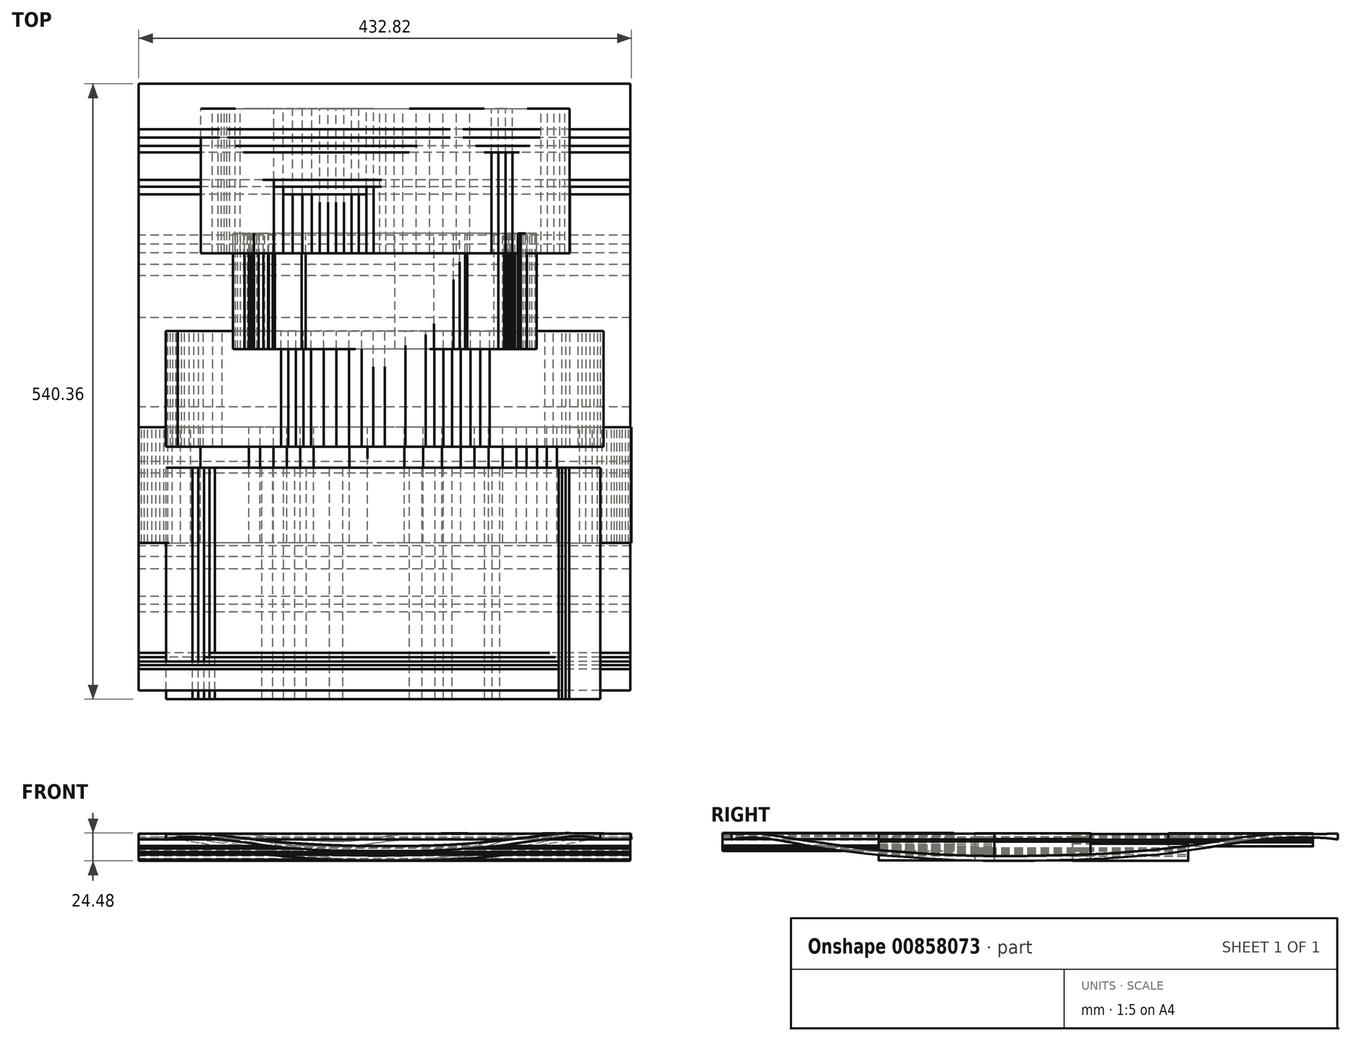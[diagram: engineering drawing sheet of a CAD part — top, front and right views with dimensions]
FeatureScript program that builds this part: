
annotation { "Feature Type Name" : "Feature", "Feature Type Description" : "" }
export const myFeature = defineFeature(function(context is Context, id is Id, definition is map)
    precondition{}
    {
        {
            var Q0;
            Q0=qCreatedBy(makeId("Top.planeOp"),FACE);
            var sketch = newSketch(context, id + "F0", { "sketchPlane" : qUnion([Q0])});
            skLineSegment(sketch, "E0", {"start": v(-117.35, 265.42) * mm, "end": v(-117.3, 265.42) * mm});
            skLineSegment(sketch, "E1", {"start": v(-117.3, 265.42) * mm, "end": v(-117.19, 265.42) * mm});
            skLineSegment(sketch, "E2", {"start": v(-117.19, 265.42) * mm, "end": v(-117.15, 265.42) * mm});
            skLineSegment(sketch, "E3", {"start": v(-117.15, 265.42) * mm, "end": v(-112.35, 265.42) * mm});
            skLineSegment(sketch, "E4", {"start": v(-112.35, 265.42) * mm, "end": v(-97.96, 264.94) * mm});
            skLineSegment(sketch, "E5", {"start": v(-97.96, 264.94) * mm, "end": v(-82, 263.83) * mm});
            skLineSegment(sketch, "E6", {"start": v(-82, 263.83) * mm, "end": v(-78.82, 263.51) * mm});
            skLineSegment(sketch, "E7", {"start": v(-78.82, 263.51) * mm, "end": v(-75.82, 263.23) * mm});
            skLineSegment(sketch, "E8", {"start": v(-75.82, 263.23) * mm, "end": v(-60.94, 260.85) * mm});
            skLineSegment(sketch, "E9", {"start": v(-60.94, 260.85) * mm, "end": v(-46.33, 257.18) * mm});
            skLineSegment(sketch, "E10", {"start": v(-46.33, 257.18) * mm, "end": v(-43.46, 256.25) * mm});
            skLineSegment(sketch, "E11", {"start": v(-43.46, 256.25) * mm, "end": v(-41.7, 255.72) * mm});
            skLineSegment(sketch, "E12", {"start": v(-41.7, 255.72) * mm, "end": v(-36.48, 253.85) * mm});
            skLineSegment(sketch, "E13", {"start": v(-36.48, 253.85) * mm, "end": v(-29.74, 250.92) * mm});
            skLineSegment(sketch, "E14", {"start": v(-29.74, 250.92) * mm, "end": v(-23.27, 247.49) * mm});
            skLineSegment(sketch, "E15", {"start": v(-23.27, 247.49) * mm, "end": v(-17.09, 243.56) * mm});
            skLineSegment(sketch, "E16", {"start": v(-17.09, 243.56) * mm, "end": v(-11.24, 239.16) * mm});
            skLineSegment(sketch, "E17", {"start": v(-11.24, 239.16) * mm, "end": v(-5.74, 234.32) * mm});
            skLineSegment(sketch, "E18", {"start": v(-5.74, 234.32) * mm, "end": v(-0.63, 229.04) * mm});
            skLineSegment(sketch, "E19", {"start": v(-0.63, 229.04) * mm, "end": v(2.96, 224.81) * mm});
            skLineSegment(sketch, "E20", {"start": v(2.96, 224.81) * mm, "end": v(4.08, 223.34) * mm});
            skLineSegment(sketch, "E21", {"start": v(4.08, 223.34) * mm, "end": v(5.7, 220.98) * mm});
            skLineSegment(sketch, "E22", {"start": v(5.7, 220.98) * mm, "end": v(9.84, 213.38) * mm});
            skLineSegment(sketch, "E23", {"start": v(9.84, 213.38) * mm, "end": v(14.01, 202.73) * mm});
            skLineSegment(sketch, "E24", {"start": v(14.01, 202.73) * mm, "end": v(16.56, 191.58) * mm});
            skLineSegment(sketch, "E25", {"start": v(16.56, 191.58) * mm, "end": v(17.43, 182.97) * mm});
            skLineSegment(sketch, "E26", {"start": v(17.43, 182.97) * mm, "end": v(17.43, 180.1) * mm});
            skLineSegment(sketch, "E27", {"start": v(17.43, 180.1) * mm, "end": v(17.43, 177.1) * mm});
            skLineSegment(sketch, "E28", {"start": v(17.43, 177.1) * mm, "end": v(16.64, 169.08) * mm});
            skLineSegment(sketch, "E29", {"start": v(16.64, 169.08) * mm, "end": v(16.48, 168.08) * mm});
            skLineSegment(sketch, "E30", {"start": v(16.48, 168.08) * mm, "end": v(15.89, 164.58) * mm});
            skLineSegment(sketch, "E31", {"start": v(15.89, 164.58) * mm, "end": v(13.52, 154.18) * mm});
            skLineSegment(sketch, "E32", {"start": v(13.52, 154.18) * mm, "end": v(9.43, 140.6) * mm});
            skLineSegment(sketch, "E33", {"start": v(9.43, 140.6) * mm, "end": v(4.22, 127.4) * mm});
            skLineSegment(sketch, "E34", {"start": v(4.22, 127.4) * mm, "end": v(-0.38, 117.78) * mm});
            skLineSegment(sketch, "E35", {"start": v(-0.38, 117.78) * mm, "end": v(-2.1, 114.67) * mm});
            skLineSegment(sketch, "E36", {"start": v(-10.33, 95.13) * mm, "end": v(-9.83, 96.82) * mm});
            skLineSegment(sketch, "E37", {"start": v(-9.83, 96.82) * mm, "end": v(-6.75, 105.13) * mm});
            skLineSegment(sketch, "E38", {"start": v(-6.75, 105.13) * mm, "end": v(-2.96, 113.12) * mm});
            skLineSegment(sketch, "E39", {"start": v(-2.96, 113.12) * mm, "end": v(-2.1, 114.67) * mm});
            skLineSegment(sketch, "E40", {"start": v(-10.57, 72.87) * mm, "end": v(-10.76, 73.74) * mm});
            skLineSegment(sketch, "E41", {"start": v(-10.76, 73.74) * mm, "end": v(-11.73, 81.05) * mm});
            skLineSegment(sketch, "E42", {"start": v(-11.73, 81.05) * mm, "end": v(-11.73, 83.49) * mm});
            skLineSegment(sketch, "E43", {"start": v(-11.73, 83.49) * mm, "end": v(-11.73, 84.95) * mm});
            skLineSegment(sketch, "E44", {"start": v(-11.73, 84.95) * mm, "end": v(-11.38, 89.35) * mm});
            skLineSegment(sketch, "E45", {"start": v(-11.38, 89.35) * mm, "end": v(-10.57, 94.17) * mm});
            skLineSegment(sketch, "E46", {"start": v(-10.57, 94.17) * mm, "end": v(-10.33, 95.13) * mm});
            skLineSegment(sketch, "E47", {"start": v(-3.12, 55.92) * mm, "end": v(-3.8, 56.87) * mm});
            skLineSegment(sketch, "E48", {"start": v(-3.8, 56.87) * mm, "end": v(-5.64, 59.85) * mm});
            skLineSegment(sketch, "E49", {"start": v(-5.64, 59.85) * mm, "end": v(-7.73, 64) * mm});
            skLineSegment(sketch, "E50", {"start": v(-7.73, 64) * mm, "end": v(-9.38, 68.36) * mm});
            skLineSegment(sketch, "E51", {"start": v(-9.38, 68.36) * mm, "end": v(-10.33, 71.73) * mm});
            skLineSegment(sketch, "E52", {"start": v(-10.33, 71.73) * mm, "end": v(-10.57, 72.87) * mm});
            skLineSegment(sketch, "E53", {"start": v(15.48, 34.95) * mm, "end": v(13.8, 36.58) * mm});
            skLineSegment(sketch, "E54", {"start": v(13.8, 36.58) * mm, "end": v(5.8, 45.1) * mm});
            skLineSegment(sketch, "E55", {"start": v(5.8, 45.1) * mm, "end": v(-1.7, 54.06) * mm});
            skLineSegment(sketch, "E56", {"start": v(-1.7, 54.06) * mm, "end": v(-3.12, 55.92) * mm});
            skLineSegment(sketch, "E57", {"start": v(15.48, 34.95) * mm, "end": v(15.65, 34.77) * mm});
            skLineSegment(sketch, "E58", {"start": v(15.65, 34.77) * mm, "end": v(17.37, 33) * mm});
            skLineSegment(sketch, "E59", {"start": v(17.37, 33) * mm, "end": v(17.54, 32.82) * mm});
            skLineSegment(sketch, "E60", {"start": v(19.48, 30.83) * mm, "end": v(19.32, 31) * mm});
            skLineSegment(sketch, "E61", {"start": v(19.32, 31) * mm, "end": v(17.7, 32.65) * mm});
            skLineSegment(sketch, "E62", {"start": v(17.7, 32.65) * mm, "end": v(17.54, 32.82) * mm});
            skLineSegment(sketch, "E63", {"start": v(19.48, 30.83) * mm, "end": v(21.7, 28.6) * mm});
            skLineSegment(sketch, "E64", {"start": v(21.7, 28.6) * mm, "end": v(28.13, 21.67) * mm});
            skLineSegment(sketch, "E65", {"start": v(28.13, 21.67) * mm, "end": v(36.2, 12) * mm});
            skLineSegment(sketch, "E66", {"start": v(36.2, 12) * mm, "end": v(43.68, 1.88) * mm});
            skLineSegment(sketch, "E67", {"start": v(43.68, 1.88) * mm, "end": v(48.9, -6) * mm});
            skLineSegment(sketch, "E68", {"start": v(48.9, -6) * mm, "end": v(50.53, -8.7) * mm});
            skLineSegment(sketch, "E69", {"start": v(50.53, -8.7) * mm, "end": v(52.29, -11.77) * mm});
            skLineSegment(sketch, "E70", {"start": v(52.29, -11.77) * mm, "end": v(57, -21.33) * mm});
            skLineSegment(sketch, "E71", {"start": v(57, -21.33) * mm, "end": v(62.25, -34.49) * mm});
            skLineSegment(sketch, "E72", {"start": v(62.25, -34.49) * mm, "end": v(66.25, -48.08) * mm});
            skLineSegment(sketch, "E73", {"start": v(66.25, -48.08) * mm, "end": v(68.46, -58.5) * mm});
            skLineSegment(sketch, "E74", {"start": v(68.46, -58.5) * mm, "end": v(68.98, -62.01) * mm});
            skLineSegment(sketch, "E75", {"start": v(68.98, -62.01) * mm, "end": v(69.27, -64.04) * mm});
            skLineSegment(sketch, "E76", {"start": v(69.27, -64.04) * mm, "end": v(70.32, -74.23) * mm});
            skLineSegment(sketch, "E77", {"start": v(70.32, -74.23) * mm, "end": v(70.76, -83.45) * mm});
            skLineSegment(sketch, "E78", {"start": v(70.76, -83.45) * mm, "end": v(70.76, -86.52) * mm});
            skLineSegment(sketch, "E79", {"start": v(70.76, -86.52) * mm, "end": v(70.76, -89.59) * mm});
            skLineSegment(sketch, "E80", {"start": v(70.76, -89.59) * mm, "end": v(70.32, -98.8) * mm});
            skLineSegment(sketch, "E81", {"start": v(70.32, -98.8) * mm, "end": v(68.99, -110.98) * mm});
            skLineSegment(sketch, "E82", {"start": v(68.99, -110.98) * mm, "end": v(66.78, -122.99) * mm});
            skLineSegment(sketch, "E83", {"start": v(66.78, -122.99) * mm, "end": v(63.72, -134.8) * mm});
            skLineSegment(sketch, "E84", {"start": v(63.72, -134.8) * mm, "end": v(59.81, -146.35) * mm});
            skLineSegment(sketch, "E85", {"start": v(59.81, -146.35) * mm, "end": v(55.08, -157.61) * mm});
            skLineSegment(sketch, "E86", {"start": v(55.08, -157.61) * mm, "end": v(49.52, -168.53) * mm});
            skLineSegment(sketch, "E87", {"start": v(49.52, -168.53) * mm, "end": v(44.85, -176.48) * mm});
            skLineSegment(sketch, "E88", {"start": v(44.85, -176.48) * mm, "end": v(43.17, -179.05) * mm});
            skLineSegment(sketch, "E89", {"start": v(43.17, -179.05) * mm, "end": v(40.83, -182.6) * mm});
            skLineSegment(sketch, "E90", {"start": v(40.83, -182.6) * mm, "end": v(33.17, -192.84) * mm});
            skLineSegment(sketch, "E91", {"start": v(33.17, -192.84) * mm, "end": v(22.02, -205.57) * mm});
            skLineSegment(sketch, "E92", {"start": v(22.02, -205.57) * mm, "end": v(9.8, -217.2) * mm});
            skLineSegment(sketch, "E93", {"start": v(9.8, -217.2) * mm, "end": v(-3.38, -227.64) * mm});
            skLineSegment(sketch, "E94", {"start": v(-3.38, -227.64) * mm, "end": v(-17.46, -236.86) * mm});
            skLineSegment(sketch, "E95", {"start": v(-17.46, -236.86) * mm, "end": v(-32.35, -244.77) * mm});
            skLineSegment(sketch, "E96", {"start": v(-32.35, -244.77) * mm, "end": v(-47.95, -251.32) * mm});
            skLineSegment(sketch, "E97", {"start": v(-47.95, -251.32) * mm, "end": v(-60.08, -255.36) * mm});
            skLineSegment(sketch, "E98", {"start": v(-60.08, -255.36) * mm, "end": v(-64.2, -256.46) * mm});
            skLineSegment(sketch, "E99", {"start": v(-64.2, -256.46) * mm, "end": v(-68.82, -257.57) * mm});
            skLineSegment(sketch, "E100", {"start": v(-68.82, -257.57) * mm, "end": v(-82.83, -260.37) * mm});
            skLineSegment(sketch, "E101", {"start": v(-82.83, -260.37) * mm, "end": v(-101.65, -263.17) * mm});
            skLineSegment(sketch, "E102", {"start": v(-101.65, -263.17) * mm, "end": v(-120.6, -264.86) * mm});
            skLineSegment(sketch, "E103", {"start": v(-120.6, -264.86) * mm, "end": v(-134.88, -265.42) * mm});
            skLineSegment(sketch, "E104", {"start": v(-134.88, -265.42) * mm, "end": v(-139.63, -265.42) * mm});
            skLineSegment(sketch, "E105", {"start": v(-139.63, -265.42) * mm, "end": v(-141.04, -265.42) * mm});
            skLineSegment(sketch, "E106", {"start": v(-141.04, -265.42) * mm, "end": v(-144.77, -265.38) * mm});
            skLineSegment(sketch, "E107", {"start": v(-144.77, -265.38) * mm, "end": v(-145.24, -265.37) * mm});
            skLineSegment(sketch, "E108", {"start": v(-145.24, -265.37) * mm, "end": v(-145.37, -265.37) * mm});
            skLineSegment(sketch, "E109", {"start": v(-145.37, -265.37) * mm, "end": v(-146.47, -265.37) * mm});
            skLineSegment(sketch, "E110", {"start": v(-146.47, -265.37) * mm, "end": v(-146.83, -265.37) * mm});
            skLineSegment(sketch, "E111", {"start": v(-146.83, -265.37) * mm, "end": v(-152.93, -265.37) * mm});
            skLineSegment(sketch, "E112", {"start": v(-152.93, -265.37) * mm, "end": v(-171.22, -264.53) * mm});
            skLineSegment(sketch, "E113", {"start": v(-171.22, -264.53) * mm, "end": v(-191.46, -262.56) * mm});
            skLineSegment(sketch, "E114", {"start": v(-191.46, -262.56) * mm, "end": v(-195.48, -262) * mm});
            skLineSegment(sketch, "E115", {"start": v(-195.48, -262) * mm, "end": v(-198.88, -261.62) * mm});
            skLineSegment(sketch, "E116", {"start": v(-198.88, -261.62) * mm, "end": v(-209, -260.03) * mm});
            skLineSegment(sketch, "E117", {"start": v(-209, -260.03) * mm, "end": v(-222.3, -257.15) * mm});
            skLineSegment(sketch, "E118", {"start": v(-222.3, -257.15) * mm, "end": v(-235.35, -253.4) * mm});
            skLineSegment(sketch, "E119", {"start": v(-235.35, -253.4) * mm, "end": v(-248.1, -248.77) * mm});
            skLineSegment(sketch, "E120", {"start": v(-248.1, -248.77) * mm, "end": v(-260.5, -243.3) * mm});
            skLineSegment(sketch, "E121", {"start": v(-260.5, -243.3) * mm, "end": v(-272.53, -236.98) * mm});
            skLineSegment(sketch, "E122", {"start": v(-272.53, -236.98) * mm, "end": v(-284.12, -229.86) * mm});
            skLineSegment(sketch, "E123", {"start": v(-284.12, -229.86) * mm, "end": v(-292.53, -224) * mm});
            skLineSegment(sketch, "E124", {"start": v(-292.53, -224) * mm, "end": v(-295.24, -221.94) * mm});
            skLineSegment(sketch, "E125", {"start": v(-295.24, -221.94) * mm, "end": v(-297.42, -220.16) * mm});
            skLineSegment(sketch, "E126", {"start": v(-297.42, -220.16) * mm, "end": v(-303.74, -214.56) * mm});
            skLineSegment(sketch, "E127", {"start": v(-303.74, -214.56) * mm, "end": v(-311.75, -206.7) * mm});
            skLineSegment(sketch, "E128", {"start": v(-311.75, -206.7) * mm, "end": v(-319.24, -198.37) * mm});
            skLineSegment(sketch, "E129", {"start": v(-319.24, -198.37) * mm, "end": v(-326.2, -189.6) * mm});
            skLineSegment(sketch, "E130", {"start": v(-326.2, -189.6) * mm, "end": v(-332.61, -180.43) * mm});
            skLineSegment(sketch, "E131", {"start": v(-332.61, -180.43) * mm, "end": v(-338.44, -170.87) * mm});
            skLineSegment(sketch, "E132", {"start": v(-338.44, -170.87) * mm, "end": v(-343.69, -160.94) * mm});
            skLineSegment(sketch, "E133", {"start": v(-343.69, -160.94) * mm, "end": v(-347.24, -153.28) * mm});
            skLineSegment(sketch, "E134", {"start": v(-347.24, -153.28) * mm, "end": v(-348.32, -150.69) * mm});
            skLineSegment(sketch, "E135", {"start": v(-348.32, -150.69) * mm, "end": v(-349.96, -146.83) * mm});
            skLineSegment(sketch, "E136", {"start": v(-349.96, -146.83) * mm, "end": v(-354.09, -134.92) * mm});
            skLineSegment(sketch, "E137", {"start": v(-354.09, -134.92) * mm, "end": v(-358.24, -118.7) * mm});
            skLineSegment(sketch, "E138", {"start": v(-358.24, -118.7) * mm, "end": v(-360.75, -102.15) * mm});
            skLineSegment(sketch, "E139", {"start": v(-360.75, -102.15) * mm, "end": v(-361.6, -89.58) * mm});
            skLineSegment(sketch, "E140", {"start": v(-361.6, -89.58) * mm, "end": v(-361.6, -85.39) * mm});
            skLineSegment(sketch, "E141", {"start": v(-361.6, -85.39) * mm, "end": v(-361.6, -82.05) * mm});
            skLineSegment(sketch, "E142", {"start": v(-361.6, -82.05) * mm, "end": v(-361.06, -72.04) * mm});
            skLineSegment(sketch, "E143", {"start": v(-361.06, -72.04) * mm, "end": v(-359.82, -60.98) * mm});
            skLineSegment(sketch, "E144", {"start": v(-359.82, -60.98) * mm, "end": v(-359.46, -58.78) * mm});
            skLineSegment(sketch, "E145", {"start": v(-359.46, -58.78) * mm, "end": v(-358.95, -55.44) * mm});
            skLineSegment(sketch, "E146", {"start": v(-358.95, -55.44) * mm, "end": v(-356.8, -45.5) * mm});
            skLineSegment(sketch, "E147", {"start": v(-356.8, -45.5) * mm, "end": v(-352.97, -32.52) * mm});
            skLineSegment(sketch, "E148", {"start": v(-352.97, -32.52) * mm, "end": v(-347.98, -19.95) * mm});
            skLineSegment(sketch, "E149", {"start": v(-347.98, -19.95) * mm, "end": v(-343.53, -10.8) * mm});
            skLineSegment(sketch, "E150", {"start": v(-343.53, -10.8) * mm, "end": v(-341.87, -7.86) * mm});
            skLineSegment(sketch, "E151", {"start": v(-341.87, -7.86) * mm, "end": v(-340.12, -4.94) * mm});
            skLineSegment(sketch, "E152", {"start": v(-340.12, -4.94) * mm, "end": v(-334.5, 3.58) * mm});
            skLineSegment(sketch, "E153", {"start": v(-334.5, 3.58) * mm, "end": v(-326.36, 14.48) * mm});
            skLineSegment(sketch, "E154", {"start": v(-326.36, 14.48) * mm, "end": v(-317.5, 24.79) * mm});
            skLineSegment(sketch, "E155", {"start": v(-317.5, 24.79) * mm, "end": v(-310.42, 32.14) * mm});
            skLineSegment(sketch, "E156", {"start": v(-310.42, 32.14) * mm, "end": v(-307.95, 34.48) * mm});
            skLineSegment(sketch, "E157", {"start": v(-285.83, 59.86) * mm, "end": v(-287.02, 58.12) * mm});
            skLineSegment(sketch, "E158", {"start": v(-287.02, 58.12) * mm, "end": v(-290.79, 53.03) * mm});
            skLineSegment(sketch, "E159", {"start": v(-290.79, 53.03) * mm, "end": v(-296.13, 46.51) * mm});
            skLineSegment(sketch, "E160", {"start": v(-296.13, 46.51) * mm, "end": v(-301.86, 40.32) * mm});
            skLineSegment(sketch, "E161", {"start": v(-301.86, 40.32) * mm, "end": v(-306.38, 35.9) * mm});
            skLineSegment(sketch, "E162", {"start": v(-306.38, 35.9) * mm, "end": v(-307.95, 34.48) * mm});
            skLineSegment(sketch, "E163", {"start": v(-278.83, 80.84) * mm, "end": v(-278.96, 79.45) * mm});
            skLineSegment(sketch, "E164", {"start": v(-278.96, 79.45) * mm, "end": v(-279.68, 75.32) * mm});
            skLineSegment(sketch, "E165", {"start": v(-279.68, 75.32) * mm, "end": v(-281.14, 69.95) * mm});
            skLineSegment(sketch, "E166", {"start": v(-281.14, 69.95) * mm, "end": v(-283.2, 64.78) * mm});
            skLineSegment(sketch, "E167", {"start": v(-283.2, 64.78) * mm, "end": v(-285.1, 61.05) * mm});
            skLineSegment(sketch, "E168", {"start": v(-285.1, 61.05) * mm, "end": v(-285.83, 59.86) * mm});
            skLineSegment(sketch, "E169", {"start": v(-280.35, 97.83) * mm, "end": v(-280.06, 96.82) * mm});
            skLineSegment(sketch, "E170", {"start": v(-280.06, 96.82) * mm, "end": v(-279.04, 91.67) * mm});
            skLineSegment(sketch, "E171", {"start": v(-279.04, 91.67) * mm, "end": v(-278.6, 86.96) * mm});
            skLineSegment(sketch, "E172", {"start": v(-278.6, 86.96) * mm, "end": v(-278.6, 85.39) * mm});
            skLineSegment(sketch, "E173", {"start": v(-278.6, 85.39) * mm, "end": v(-278.6, 84.25) * mm});
            skLineSegment(sketch, "E174", {"start": v(-278.6, 84.25) * mm, "end": v(-278.8, 81.21) * mm});
            skLineSegment(sketch, "E175", {"start": v(-278.8, 81.21) * mm, "end": v(-278.83, 80.84) * mm});
            skLineSegment(sketch, "E176", {"start": v(-288.21, 116.43) * mm, "end": v(-287.43, 114.94) * mm});
            skLineSegment(sketch, "E177", {"start": v(-287.43, 114.94) * mm, "end": v(-283.9, 107.3) * mm});
            skLineSegment(sketch, "E178", {"start": v(-283.9, 107.3) * mm, "end": v(-280.88, 99.43) * mm});
            skLineSegment(sketch, "E179", {"start": v(-280.88, 99.43) * mm, "end": v(-280.35, 97.83) * mm});
            skLineSegment(sketch, "E180", {"start": v(-288.21, 116.43) * mm, "end": v(-289, 118.06) * mm});
            skLineSegment(sketch, "E181", {"start": v(-289, 118.06) * mm, "end": v(-296.24, 134.68) * mm});
            skLineSegment(sketch, "E182", {"start": v(-296.24, 134.68) * mm, "end": v(-296.89, 136.36) * mm});
            skLineSegment(sketch, "E183", {"start": v(-296.89, 136.36) * mm, "end": v(-298, 138.97) * mm});
            skLineSegment(sketch, "E184", {"start": v(-298, 138.97) * mm, "end": v(-300.89, 146.98) * mm});
            skLineSegment(sketch, "E185", {"start": v(-300.89, 146.98) * mm, "end": v(-303.9, 157.9) * mm});
            skLineSegment(sketch, "E186", {"start": v(-303.9, 157.9) * mm, "end": v(-305.92, 169.03) * mm});
            skLineSegment(sketch, "E187", {"start": v(-305.92, 169.03) * mm, "end": v(-306.8, 177.5) * mm});
            skLineSegment(sketch, "E188", {"start": v(-306.8, 177.5) * mm, "end": v(-306.92, 180.33) * mm});
            skLineSegment(sketch, "E189", {"start": v(-306.92, 180.33) * mm, "end": v(-306.92, 180.41) * mm});
            skLineSegment(sketch, "E190", {"start": v(-306.92, 180.41) * mm, "end": v(-306.93, 181.08) * mm});
            skLineSegment(sketch, "E191", {"start": v(-306.93, 181.08) * mm, "end": v(-306.93, 181.3) * mm});
            skLineSegment(sketch, "E192", {"start": v(-306.93, 181.3) * mm, "end": v(-306.93, 182.6) * mm});
            skLineSegment(sketch, "E193", {"start": v(-306.93, 182.6) * mm, "end": v(-306.63, 186.45) * mm});
            skLineSegment(sketch, "E194", {"start": v(-306.63, 186.45) * mm, "end": v(-305.74, 191.48) * mm});
            skLineSegment(sketch, "E195", {"start": v(-305.74, 191.48) * mm, "end": v(-304.3, 196.33) * mm});
            skLineSegment(sketch, "E196", {"start": v(-304.3, 196.33) * mm, "end": v(-302.3, 200.97) * mm});
            skLineSegment(sketch, "E197", {"start": v(-302.3, 200.97) * mm, "end": v(-299.78, 205.36) * mm});
            skLineSegment(sketch, "E198", {"start": v(-299.78, 205.36) * mm, "end": v(-296.77, 209.44) * mm});
            skLineSegment(sketch, "E199", {"start": v(-296.77, 209.44) * mm, "end": v(-293.29, 213.16) * mm});
            skLineSegment(sketch, "E200", {"start": v(-293.29, 213.16) * mm, "end": v(-290.38, 215.72) * mm});
            skLineSegment(sketch, "E201", {"start": v(-290.38, 215.72) * mm, "end": v(-289.35, 216.5) * mm});
            skLineSegment(sketch, "E202", {"start": v(-289.35, 216.5) * mm, "end": v(-288, 217.54) * mm});
            skLineSegment(sketch, "E203", {"start": v(-288, 217.54) * mm, "end": v(-283.58, 220.23) * mm});
            skLineSegment(sketch, "E204", {"start": v(-283.58, 220.23) * mm, "end": v(-277.32, 222.95) * mm});
            skLineSegment(sketch, "E205", {"start": v(-277.32, 222.95) * mm, "end": v(-270.7, 224.62) * mm});
            skLineSegment(sketch, "E206", {"start": v(-270.7, 224.62) * mm, "end": v(-265.56, 225.18) * mm});
            skLineSegment(sketch, "E207", {"start": v(-265.56, 225.18) * mm, "end": v(-263.85, 225.18) * mm});
            skLineSegment(sketch, "E208", {"start": v(-263.85, 225.18) * mm, "end": v(-262.53, 225.18) * mm});
            skLineSegment(sketch, "E209", {"start": v(-262.53, 225.18) * mm, "end": v(-258.58, 224.85) * mm});
            skLineSegment(sketch, "E210", {"start": v(-258.58, 224.85) * mm, "end": v(-254.24, 224.07) * mm});
            skLineSegment(sketch, "E211", {"start": v(-254.24, 224.07) * mm, "end": v(-253.39, 223.85) * mm});
            skLineSegment(sketch, "E212", {"start": v(-253.39, 223.85) * mm, "end": v(-252, 223.4) * mm});
            skLineSegment(sketch, "E213", {"start": v(-252, 223.4) * mm, "end": v(-245.26, 220.58) * mm});
            skLineSegment(sketch, "E214", {"start": v(-245.26, 220.58) * mm, "end": v(-238.9, 217) * mm});
            skLineSegment(sketch, "E215", {"start": v(-238.9, 217) * mm, "end": v(-237.7, 216.17) * mm});
            skLineSegment(sketch, "E216", {"start": v(-237.7, 216.17) * mm, "end": v(-236.6, 215.43) * mm});
            skLineSegment(sketch, "E217", {"start": v(-236.6, 215.43) * mm, "end": v(-226.06, 207.52) * mm});
            skLineSegment(sketch, "E218", {"start": v(-226.06, 207.52) * mm, "end": v(-225.05, 206.67) * mm});
            skLineSegment(sketch, "E219", {"start": v(-210.67, 197.02) * mm, "end": v(-211.96, 197.67) * mm});
            skLineSegment(sketch, "E220", {"start": v(-211.96, 197.67) * mm, "end": v(-218.15, 201.4) * mm});
            skLineSegment(sketch, "E221", {"start": v(-218.15, 201.4) * mm, "end": v(-223.95, 205.73) * mm});
            skLineSegment(sketch, "E222", {"start": v(-223.95, 205.73) * mm, "end": v(-225.05, 206.67) * mm});
            skLineSegment(sketch, "E223", {"start": v(-194.07, 193.77) * mm, "end": v(-194.28, 193.75) * mm});
            skLineSegment(sketch, "E224", {"start": v(-194.28, 193.75) * mm, "end": v(-196.07, 193.66) * mm});
            skLineSegment(sketch, "E225", {"start": v(-196.07, 193.66) * mm, "end": v(-196.66, 193.66) * mm});
            skLineSegment(sketch, "E226", {"start": v(-196.66, 193.66) * mm, "end": v(-198.46, 193.66) * mm});
            skLineSegment(sketch, "E227", {"start": v(-198.46, 193.66) * mm, "end": v(-203.87, 194.51) * mm});
            skLineSegment(sketch, "E228", {"start": v(-203.87, 194.51) * mm, "end": v(-209.59, 196.46) * mm});
            skLineSegment(sketch, "E229", {"start": v(-209.59, 196.46) * mm, "end": v(-210.67, 197.02) * mm});
            skLineSegment(sketch, "E230", {"start": v(-173.23, 213.17) * mm, "end": v(-173.4, 212.22) * mm});
            skLineSegment(sketch, "E231", {"start": v(-173.4, 212.22) * mm, "end": v(-174.26, 209.43) * mm});
            skLineSegment(sketch, "E232", {"start": v(-174.26, 209.43) * mm, "end": v(-175.85, 205.96) * mm});
            skLineSegment(sketch, "E233", {"start": v(-175.85, 205.96) * mm, "end": v(-177.94, 202.82) * mm});
            skLineSegment(sketch, "E234", {"start": v(-177.94, 202.82) * mm, "end": v(-180.47, 200.06) * mm});
            skLineSegment(sketch, "E235", {"start": v(-180.47, 200.06) * mm, "end": v(-183.4, 197.73) * mm});
            skLineSegment(sketch, "E236", {"start": v(-183.4, 197.73) * mm, "end": v(-186.69, 195.87) * mm});
            skLineSegment(sketch, "E237", {"start": v(-186.69, 195.87) * mm, "end": v(-190.26, 194.54) * mm});
            skLineSegment(sketch, "E238", {"start": v(-190.26, 194.54) * mm, "end": v(-193.1, 193.89) * mm});
            skLineSegment(sketch, "E239", {"start": v(-193.1, 193.89) * mm, "end": v(-194.07, 193.77) * mm});
            skLineSegment(sketch, "E240", {"start": v(-172.31, 265.42) * mm, "end": v(-173.23, 213.17) * mm});
            skLineSegment(sketch, "E241", {"start": v(-117.35, 265.42) * mm, "end": v(-172.31, 265.42) * mm});
            skLineSegment(sketch, "E242", {"start": v(361.6, -105.85) * mm, "end": v(360.96, -105.85) * mm});
            skSolve(sketch);
        }
        {
            var Q0;
            Q0=qCreatedBy(makeId("Top.planeOp"),FACE);
            var sketch = newSketch(context, id + "F1", { "sketchPlane" : qUnion([Q0])});
            skLineSegment(sketch, "E243.bottom", {"start": v(-361.93, -265.58) * mm, "end": v(70.9, -265.58) * mm, "construction": true});
            skLineSegment(sketch, "E243.top", {"start": v(-361.93, 265.47) * mm, "end": v(70.9, 265.47) * mm, "construction": true});
            skLineSegment(sketch, "E243.left", {"start": v(-361.93, -265.58) * mm, "end": v(-361.93, 265.47) * mm, "construction": true});
            skLineSegment(sketch, "E243.right", {"start": v(70.9, -265.58) * mm, "end": v(70.9, 265.47) * mm, "construction": true});
            skLineSegment(sketch, "E244", {"start": v(-145.52, 265.47) * mm, "end": v(-145.52, -265.58) * mm, "construction": true});
            skLineSegment(sketch, "E245", {"start": v(-361.93, 181.33) * mm, "end": v(70.9, 181.33) * mm, "construction": true});
            skLineSegment(sketch, "E246", {"start": v(-361.93, 84.5) * mm, "end": v(70.9, 84.5) * mm, "construction": true});
            skLineSegment(sketch, "E247", {"start": v(-361.93, -1.23) * mm, "end": v(70.9, -1.23) * mm, "construction": true});
            skPoint(sketch, "E247.endSnap0", {"position": v(70.9, -0.06) * mm});
            skLineSegment(sketch, "E248", {"start": v(-361.93, -85.78) * mm, "end": v(70.9, -85.78) * mm, "construction": true});
            skLineSegment(sketch, "E249", {"start": v(-361.93, -172.14) * mm, "end": v(70.9, -172.14) * mm, "construction": true});
            skSolve(sketch);
        }
        {
            var Q0;
            Q0=sQuery(id+"F1.wireOp",EDGE,"E245");
            cPoint(context, id + "F2", {"entities" : qUnion([Q0]), "parameter" : 0.5});
        }
        {
            var Q0;
            Q0=sQuery(id+"F1.wireOp",EDGE,"E244");
            var Q1;
            Q1 = qCreatedBy(id + "F2" ,VERTEX);
            cPlane(context, id + "F3", {"entities" : qUnion([Q0, Q1]), "cplaneType" : CPlaneType.LINE_POINT, "offset" : 25.4 * mm, "width" : 152.4 * mm, "height" : 152.4 * mm});
        }
        {
            var Q0;
            Q0=sQuery(id+"F1.wireOp",EDGE,"E246");
            cPoint(context, id + "F4", {"entities" : qUnion([Q0]), "parameter" : 0.5});
        }
        {
            var Q0;
            Q0=sQuery(id+"F1.wireOp",EDGE,"E244");
            var Q1;
            Q1 = qCreatedBy(id + "F4" ,VERTEX);
            cPlane(context, id + "F5", {"entities" : qUnion([Q0, Q1]), "cplaneType" : CPlaneType.LINE_POINT, "offset" : 25.4 * mm, "width" : 152.4 * mm, "height" : 152.4 * mm});
        }
        {
            var Q0;
            Q0=qCreatedBy(id+"F5.planeOp",FACE);
            var sketch = newSketch(context, id + "F6", { "sketchPlane" : qUnion([Q0])});
            skLineSegment(sketch, "E250.0", {"start": v(-77.03, -13.38) * mm, "end": v(-85.36, -15.2) * mm});
            skLineSegment(sketch, "E250.1", {"start": v(-68.79, -11.26) * mm, "end": v(-77.03, -13.38) * mm});
            skLineSegment(sketch, "E250.2", {"start": v(-57.14, -7.86) * mm, "end": v(-68.79, -11.26) * mm});
            skLineSegment(sketch, "E250.3", {"start": v(-45.53, -4.33) * mm, "end": v(-57.14, -7.86) * mm});
            skLineSegment(sketch, "E250.4", {"start": v(-40.68, -2.92) * mm, "end": v(-45.53, -4.33) * mm});
            skLineSegment(sketch, "E250.5", {"start": v(-35.8, -1.69) * mm, "end": v(-40.68, -2.92) * mm});
            skLineSegment(sketch, "E250.6", {"start": v(-33.35, -1.17) * mm, "end": v(-35.8, -1.69) * mm});
            skLineSegment(sketch, "E250.7", {"start": v(-30.88, -0.74) * mm, "end": v(-33.35, -1.17) * mm});
            skLineSegment(sketch, "E250.8", {"start": v(-28.4, -0.42) * mm, "end": v(-30.88, -0.74) * mm});
            skLineSegment(sketch, "E250.9", {"start": v(-25.89, -0.2) * mm, "end": v(-28.4, -0.42) * mm});
            skLineSegment(sketch, "E250.10", {"start": v(-23.17, -0.15) * mm, "end": v(-25.89, -0.2) * mm});
            skLineSegment(sketch, "E250.11", {"start": v(-20.44, -0.2) * mm, "end": v(-23.17, -0.15) * mm});
            skLineSegment(sketch, "E250.12", {"start": v(-12.03, -0.2) * mm, "end": v(-20.44, -0.2) * mm});
            skLineSegment(sketch, "E250.13", {"start": v(-12.03, -0.2) * mm, "end": v(-12.03, -5.37) * mm});
            skLineSegment(sketch, "E250.14", {"start": v(-13.3, -4.77) * mm, "end": v(-12.03, -5.27) * mm});
            skLineSegment(sketch, "E250.15", {"start": v(-16.17, -3.82) * mm, "end": v(-13.3, -4.77) * mm});
            skLineSegment(sketch, "E250.16", {"start": v(-18.04, -3.36) * mm, "end": v(-16.17, -3.82) * mm});
            skLineSegment(sketch, "E250.17", {"start": v(-19.94, -3.05) * mm, "end": v(-18.04, -3.36) * mm});
            skLineSegment(sketch, "E250.18", {"start": v(-21.85, -2.88) * mm, "end": v(-19.94, -3.05) * mm});
            skLineSegment(sketch, "E250.19", {"start": v(-23.77, -2.87) * mm, "end": v(-21.85, -2.88) * mm});
            skLineSegment(sketch, "E250.20", {"start": v(-25.68, -3.03) * mm, "end": v(-23.77, -2.87) * mm});
            skLineSegment(sketch, "E250.21", {"start": v(-27.58, -3.3) * mm, "end": v(-25.68, -3.03) * mm});
            skLineSegment(sketch, "E250.22", {"start": v(-31.35, -4.07) * mm, "end": v(-27.58, -3.3) * mm});
            skLineSegment(sketch, "E250.23", {"start": v(-36.56, -5.15) * mm, "end": v(-31.35, -4.07) * mm});
            skLineSegment(sketch, "E250.24", {"start": v(-41.74, -6.37) * mm, "end": v(-36.56, -5.15) * mm});
            skLineSegment(sketch, "E250.25", {"start": v(-45.61, -7.5) * mm, "end": v(-41.74, -6.37) * mm});
            skLineSegment(sketch, "E250.26", {"start": v(-49.44, -8.8) * mm, "end": v(-45.61, -7.5) * mm});
            skLineSegment(sketch, "E250.27", {"start": v(-57.07, -11.46) * mm, "end": v(-49.44, -8.8) * mm});
            skLineSegment(sketch, "E250.28", {"start": v(-62.66, -13.24) * mm, "end": v(-57.07, -11.46) * mm});
            skLineSegment(sketch, "E250.29", {"start": v(-68.3, -14.88) * mm, "end": v(-62.66, -13.24) * mm});
            skLineSegment(sketch, "E250.30", {"start": v(-73.98, -16.36) * mm, "end": v(-68.3, -14.88) * mm});
            skLineSegment(sketch, "E250.31", {"start": v(-79.7, -17.7) * mm, "end": v(-73.98, -16.36) * mm});
            skLineSegment(sketch, "E250.32", {"start": v(-88, -19.37) * mm, "end": v(-79.7, -17.7) * mm});
            skLineSegment(sketch, "E250.33", {"start": v(-85.36, -15.2) * mm, "end": v(-89.54, -15.98) * mm});
            skLineSegment(sketch, "E250.34", {"start": v(-92.18, -20.08) * mm, "end": v(-88, -19.37) * mm});
            skLineSegment(sketch, "E250.35", {"start": v(-89.54, -15.98) * mm, "end": v(-93.74, -16.67) * mm});
            skLineSegment(sketch, "E250.36", {"start": v(-96.37, -20.7) * mm, "end": v(-92.18, -20.08) * mm});
            skLineSegment(sketch, "E250.37", {"start": v(-93.74, -16.67) * mm, "end": v(-97.96, -17.28) * mm});
            skLineSegment(sketch, "E250.38", {"start": v(-101.74, -21.38) * mm, "end": v(-96.37, -20.7) * mm});
            skLineSegment(sketch, "E250.39", {"start": v(-97.96, -17.28) * mm, "end": v(-102.19, -17.8) * mm});
            skLineSegment(sketch, "E250.40", {"start": v(-102.19, -17.8) * mm, "end": v(-107.53, -18.34) * mm});
            skLineSegment(sketch, "E250.41", {"start": v(-107.11, -21.95) * mm, "end": v(-101.74, -21.38) * mm});
            skLineSegment(sketch, "E250.42", {"start": v(-107.53, -18.34) * mm, "end": v(-112.88, -18.75) * mm});
            skLineSegment(sketch, "E250.43", {"start": v(-112.5, -22.41) * mm, "end": v(-107.11, -21.95) * mm});
            skLineSegment(sketch, "E250.44", {"start": v(-112.88, -18.75) * mm, "end": v(-118.24, -19.06) * mm});
            skLineSegment(sketch, "E250.45", {"start": v(-117.9, -22.8) * mm, "end": v(-112.5, -22.41) * mm});
            skLineSegment(sketch, "E250.46", {"start": v(-118.24, -19.06) * mm, "end": v(-123.61, -19.28) * mm});
            skLineSegment(sketch, "E250.47", {"start": v(-124.7, -23.17) * mm, "end": v(-117.9, -22.8) * mm});
            skLineSegment(sketch, "E250.48", {"start": v(-123.61, -19.28) * mm, "end": v(-134.35, -19.47) * mm});
            skLineSegment(sketch, "E250.49", {"start": v(-131.52, -23.45) * mm, "end": v(-124.7, -23.17) * mm});
            skLineSegment(sketch, "E250.50", {"start": v(-134.35, -19.47) * mm, "end": v(-145.1, -19.43) * mm});
            skLineSegment(sketch, "E250.51", {"start": v(-138.34, -23.62) * mm, "end": v(-131.52, -23.45) * mm});
            skLineSegment(sketch, "E250.52", {"start": v(-145.16, -23.7) * mm, "end": v(-138.34, -23.62) * mm});
            skLineSegment(sketch, "E250.53", {"start": v(-145.1, -19.43) * mm, "end": v(-155.5, -19.22) * mm});
            skLineSegment(sketch, "E250.54", {"start": v(-152.65, -23.66) * mm, "end": v(-145.16, -23.7) * mm});
            skLineSegment(sketch, "E250.55", {"start": v(-160.14, -23.5) * mm, "end": v(-152.65, -23.66) * mm});
            skLineSegment(sketch, "E250.56", {"start": v(-155.5, -19.22) * mm, "end": v(-165.89, -18.83) * mm});
            skLineSegment(sketch, "E250.57", {"start": v(-167.75, -23.2) * mm, "end": v(-160.14, -23.5) * mm});
            skLineSegment(sketch, "E250.58", {"start": v(-165.89, -18.83) * mm, "end": v(-176.26, -18.23) * mm});
            skLineSegment(sketch, "E250.59", {"start": v(-175.35, -22.75) * mm, "end": v(-167.75, -23.2) * mm});
            skLineSegment(sketch, "E250.60", {"start": v(-182.94, -22.13) * mm, "end": v(-175.35, -22.75) * mm});
            skLineSegment(sketch, "E250.61", {"start": v(-176.26, -18.23) * mm, "end": v(-186.63, -17.38) * mm});
            skLineSegment(sketch, "E250.62", {"start": v(-190.5, -21.3) * mm, "end": v(-182.94, -22.13) * mm});
            skLineSegment(sketch, "E250.63", {"start": v(-186.63, -17.38) * mm, "end": v(-196, -16.37) * mm});
            skLineSegment(sketch, "E250.64", {"start": v(-198.76, -20.1) * mm, "end": v(-190.5, -21.3) * mm});
            skLineSegment(sketch, "E250.65", {"start": v(-196, -16.37) * mm, "end": v(-200.67, -15.75) * mm});
            skLineSegment(sketch, "E250.66", {"start": v(-206.97, -18.59) * mm, "end": v(-198.76, -20.1) * mm});
            skLineSegment(sketch, "E250.67", {"start": v(-200.67, -15.75) * mm, "end": v(-205.32, -15.04) * mm});
            skLineSegment(sketch, "E250.68", {"start": v(-215.12, -16.8) * mm, "end": v(-206.97, -18.59) * mm});
            skLineSegment(sketch, "E250.69", {"start": v(-205.32, -15.04) * mm, "end": v(-209.96, -14.23) * mm});
            skLineSegment(sketch, "E250.70", {"start": v(-209.96, -14.23) * mm, "end": v(-214.58, -13.31) * mm});
            skLineSegment(sketch, "E250.71", {"start": v(-214.58, -13.31) * mm, "end": v(-219.17, -12.27) * mm});
            skLineSegment(sketch, "E250.72", {"start": v(-223.21, -14.75) * mm, "end": v(-215.12, -16.8) * mm});
            skLineSegment(sketch, "E250.73", {"start": v(-219.17, -12.27) * mm, "end": v(-223.72, -11.1) * mm});
            skLineSegment(sketch, "E250.74", {"start": v(-227.9, -13.46) * mm, "end": v(-223.21, -14.75) * mm});
            skLineSegment(sketch, "E250.75", {"start": v(-223.72, -11.1) * mm, "end": v(-229.77, -9.33) * mm});
            skLineSegment(sketch, "E250.76", {"start": v(-232.55, -12.08) * mm, "end": v(-227.9, -13.46) * mm});
            skLineSegment(sketch, "E250.77", {"start": v(-229.77, -9.33) * mm, "end": v(-235.77, -7.44) * mm});
            skLineSegment(sketch, "E250.78", {"start": v(-237.18, -10.61) * mm, "end": v(-232.55, -12.08) * mm});
            skLineSegment(sketch, "E250.79", {"start": v(-235.77, -7.44) * mm, "end": v(-241.78, -5.54) * mm});
            skLineSegment(sketch, "E250.80", {"start": v(-241.79, -9.06) * mm, "end": v(-237.18, -10.61) * mm});
            skLineSegment(sketch, "E250.81", {"start": v(-241.78, -5.54) * mm, "end": v(-247.81, -3.75) * mm});
            skLineSegment(sketch, "E250.82", {"start": v(-250.86, -5.96) * mm, "end": v(-241.79, -9.06) * mm});
            skLineSegment(sketch, "E250.83", {"start": v(-247.81, -3.75) * mm, "end": v(-251.94, -2.68) * mm});
            skLineSegment(sketch, "E250.84", {"start": v(-255.45, -4.67) * mm, "end": v(-250.86, -5.96) * mm});
            skLineSegment(sketch, "E250.85", {"start": v(-251.94, -2.68) * mm, "end": v(-256.11, -1.77) * mm});
            skLineSegment(sketch, "E250.86", {"start": v(-256.11, -1.77) * mm, "end": v(-260.32, -1.1) * mm});
            skLineSegment(sketch, "E250.87", {"start": v(-257.78, -4.15) * mm, "end": v(-255.45, -4.67) * mm});
            skLineSegment(sketch, "E250.88", {"start": v(-263.11, -3.42) * mm, "end": v(-260.14, -3.74) * mm});
            skLineSegment(sketch, "E250.89", {"start": v(-260.14, -3.74) * mm, "end": v(-257.78, -4.15) * mm});
            skLineSegment(sketch, "E250.90", {"start": v(-260.32, -1.1) * mm, "end": v(-264.56, -0.7) * mm});
            skLineSegment(sketch, "E250.91", {"start": v(-266.1, -3.33) * mm, "end": v(-263.11, -3.42) * mm});
            skLineSegment(sketch, "E250.92", {"start": v(-264.56, -0.7) * mm, "end": v(-268.48, -0.63) * mm});
            skLineSegment(sketch, "E250.93", {"start": v(-269.09, -3.5) * mm, "end": v(-266.1, -3.33) * mm});
            skLineSegment(sketch, "E250.94", {"start": v(-268.48, -0.63) * mm, "end": v(-272.4, -0.7) * mm});
            skLineSegment(sketch, "E250.95", {"start": v(-272.05, -3.92) * mm, "end": v(-269.09, -3.5) * mm});
            skLineSegment(sketch, "E250.96", {"start": v(-272.4, -0.7) * mm, "end": v(-278.64, -0.7) * mm});
            skLineSegment(sketch, "E250.97", {"start": v(-274.5, -4.49) * mm, "end": v(-272.05, -3.92) * mm});
            skLineSegment(sketch, "E250.98", {"start": v(-276.6, -5.11) * mm, "end": v(-274.5, -4.49) * mm});
            skLineSegment(sketch, "E250.99", {"start": v(-278.64, -5.82) * mm, "end": v(-276.6, -5.11) * mm});
            skLineSegment(sketch, "E250.100", {"start": v(-278.64, -5.82) * mm, "end": v(-278.64, -0.7) * mm});
            skPoint(sketch, "E251.48.internal.snap0", {"position": v(-32.11, -0.96) * mm});
            skFitSpline(sketch, "E251", {"points": [v(-12.03, -0.2) * mm, v(-20.44, -0.2) * mm, v(-23.17, -0.15) * mm, v(-25.89, -0.2) * mm, v(-28.06, -0.39) * mm, v(-29.63, -0.58) * mm, v(-32.66, -1.05) * mm, v(-34.57, -1.43) * mm, v(-37.6, -2.14) * mm, v(-38.24, -2.3) * mm, v(-42.64, -3.5) * mm, v(-47.77, -5.01) * mm, v(-55.38, -7.33) * mm, v(-63.25, -9.64) * mm, v(-72.91, -12.32) * mm, v(-74.84, -12.82) * mm, v(-79.74, -13.97) * mm, v(-86.3, -15.37) * mm, v(-91.64, -16.33) * mm, v(-93.17, -16.58) * mm, v(-97.07, -17.15) * mm, v(-102.19, -17.8) * mm, v(-106.04, -18.19) * mm, v(-111.74, -18.66) * mm, v(-115.56, -18.9) * mm, v(-116.76, -18.98) * mm, v(-120.93, -19.17) * mm, v(-127.84, -19.35) * mm, v(-136.42, -19.46) * mm, v(-142.08, -19.44) * mm, v(-149.15, -19.35) * mm, v(-158.82, -19.1) * mm, v(-174.38, -18.34) * mm, v(-182.4, -17.73) * mm, v(-190.82, -16.93) * mm, v(-198.33, -16.06) * mm, v(-204.32, -15.2) * mm, v(-207.64, -14.64) * mm, v(-214.22, -13.38) * mm, v(-218.33, -12.46) * mm, v(-222.73, -11.35) * mm, v(-227.11, -10.1) * mm, v(-234.43, -7.86) * mm, v(-238.77, -6.49) * mm, v(-243.79, -4.94) * mm, v(-249.18, -3.4) * mm, v(-255, -2.01) * mm, v(-256.8, -1.66) * mm, v(-261.77, -0.96) * mm, v(-266.1, -0.67) * mm, v(-270.44, -0.67) * mm, v(-274.76, -0.7) * mm, v(-277.68, -0.7) * mm, v(-278.64, -0.7) * mm], "startDerivative": vector(-383.27, -1.5) * mm, "endDerivative": vector(-98.65, -0.09) * mm});
            skLineSegment(sketch, "E252", {"start": v(-278.64, -0.7) * mm, "end": v(-278.64, -5.82) * mm});
            skFitSpline(sketch, "E253", {"points": [v(-278.64, -5.82) * mm, v(-276.6, -5.11) * mm, v(-274.5, -4.49) * mm, v(-272.05, -3.92) * mm, v(-269.09, -3.5) * mm, v(-266.1, -3.33) * mm, v(-263.11, -3.42) * mm, v(-260.14, -3.74) * mm, v(-257.78, -4.15) * mm, v(-255.45, -4.67) * mm, v(-250.86, -5.96) * mm, v(-241.79, -9.06) * mm, v(-237.18, -10.61) * mm, v(-232.55, -12.08) * mm, v(-227.9, -13.46) * mm, v(-223.21, -14.75) * mm, v(-215.12, -16.8) * mm, v(-206.97, -18.59) * mm, v(-198.76, -20.1) * mm, v(-190.5, -21.3) * mm, v(-182.94, -22.13) * mm, v(-175.35, -22.75) * mm, v(-167.75, -23.2) * mm, v(-160.14, -23.5) * mm, v(-152.65, -23.66) * mm, v(-145.16, -23.7) * mm, v(-138.34, -23.62) * mm, v(-131.52, -23.45) * mm, v(-124.7, -23.17) * mm, v(-117.9, -22.8) * mm, v(-112.5, -22.41) * mm, v(-107.11, -21.95) * mm, v(-101.74, -21.38) * mm, v(-96.37, -20.7) * mm, v(-92.18, -20.08) * mm, v(-88, -19.37) * mm, v(-79.7, -17.7) * mm, v(-73.98, -16.36) * mm, v(-68.3, -14.88) * mm, v(-62.66, -13.24) * mm, v(-57.07, -11.46) * mm, v(-49.44, -8.8) * mm, v(-45.61, -7.5) * mm, v(-41.74, -6.37) * mm, v(-36.56, -5.15) * mm, v(-31.35, -4.07) * mm, v(-27.58, -3.3) * mm, v(-25.68, -3.03) * mm, v(-23.77, -2.87) * mm, v(-21.85, -2.88) * mm, v(-19.94, -3.05) * mm, v(-18.04, -3.36) * mm, v(-16.17, -3.82) * mm, v(-13.3, -4.77) * mm, v(-12.03, -5.27) * mm], "startDerivative": vector(162.85, 58.14) * mm, "endDerivative": vector(111.62, -45.84) * mm});
            skLineSegment(sketch, "E254", {"start": v(-12.03, -0.2) * mm, "end": v(-12.03, -5.27) * mm});
            skSolve(sketch);
        }
        {
            var Q0;
            Q0=qCreatedBy(id+"F3.planeOp",FACE);
            var sketch = newSketch(context, id + "F7", { "sketchPlane" : qUnion([Q0])});
            skLineSegment(sketch, "E255.0", {"start": v(-144.49, -6.65) * mm, "end": v(-137, -5.84) * mm});
            skLineSegment(sketch, "E255.1", {"start": v(-144.49, -2.37) * mm, "end": v(-139.31, -1.64) * mm});
            skLineSegment(sketch, "E255.2", {"start": v(17.05, 0.27) * mm, "end": v(17.13, -4.8) * mm});
            skLineSegment(sketch, "E255.3", {"start": v(9.79, 0.27) * mm, "end": v(17.05, 0.27) * mm});
            skLineSegment(sketch, "E255.4", {"start": v(12.79, -4.33) * mm, "end": v(17.13, -4.8) * mm});
            skLineSegment(sketch, "E255.5", {"start": v(8.34, -3.95) * mm, "end": v(12.79, -4.33) * mm});
            skLineSegment(sketch, "E255.6", {"start": v(0.55, 0.33) * mm, "end": v(9.79, 0.27) * mm});
            skLineSegment(sketch, "E255.7", {"start": v(3.22, -3.67) * mm, "end": v(8.34, -3.95) * mm});
            skLineSegment(sketch, "E255.8", {"start": v(-2.42, -3.58) * mm, "end": v(3.22, -3.67) * mm});
            skLineSegment(sketch, "E255.9", {"start": v(-8.7, 0.27) * mm, "end": v(0.55, 0.33) * mm});
            skLineSegment(sketch, "E255.10", {"start": v(-8.06, -3.68) * mm, "end": v(-2.42, -3.58) * mm});
            skLineSegment(sketch, "E255.11", {"start": v(-17.94, -0.02) * mm, "end": v(-8.7, 0.27) * mm});
            skLineSegment(sketch, "E255.12", {"start": v(-19.35, -4.19) * mm, "end": v(-8.06, -3.68) * mm});
            skLineSegment(sketch, "E255.13", {"start": v(-27.17, -0.39) * mm, "end": v(-17.94, -0.02) * mm});
            skLineSegment(sketch, "E255.14", {"start": v(-28.72, -4.63) * mm, "end": v(-19.35, -4.19) * mm});
            skLineSegment(sketch, "E255.15", {"start": v(-33.28, -0.58) * mm, "end": v(-27.17, -0.39) * mm});
            skLineSegment(sketch, "E255.16", {"start": v(-38.1, -4.91) * mm, "end": v(-28.72, -4.63) * mm});
            skLineSegment(sketch, "E255.17", {"start": v(-39.38, -0.68) * mm, "end": v(-33.28, -0.58) * mm});
            skLineSegment(sketch, "E255.18", {"start": v(-43.2, -4.93) * mm, "end": v(-38.1, -4.91) * mm});
            skLineSegment(sketch, "E255.19", {"start": v(-45.49, -0.68) * mm, "end": v(-39.38, -0.68) * mm});
            skLineSegment(sketch, "E255.20", {"start": v(-48.3, -4.87) * mm, "end": v(-43.2, -4.93) * mm});
            skLineSegment(sketch, "E255.21", {"start": v(-51.6, -0.55) * mm, "end": v(-45.49, -0.68) * mm});
            skLineSegment(sketch, "E255.22", {"start": v(-58.49, -4.6) * mm, "end": v(-48.3, -4.87) * mm});
            skLineSegment(sketch, "E255.23", {"start": v(-65.7, 0.1) * mm, "end": v(-51.6, -0.55) * mm});
            skLineSegment(sketch, "E255.24", {"start": v(-70.55, -4.28) * mm, "end": v(-58.49, -4.6) * mm});
            skLineSegment(sketch, "E255.25", {"start": v(-76.73, 0.37) * mm, "end": v(-65.7, 0.1) * mm});
            skLineSegment(sketch, "E255.26", {"start": v(-82.62, -4.08) * mm, "end": v(-70.55, -4.28) * mm});
            skLineSegment(sketch, "E255.27", {"start": v(-87.76, 0.38) * mm, "end": v(-76.73, 0.37) * mm});
            skLineSegment(sketch, "E255.28", {"start": v(-94.35, -4.08) * mm, "end": v(-82.62, -4.08) * mm});
            skLineSegment(sketch, "E255.29", {"start": v(-109.84, 0.1) * mm, "end": v(-87.76, 0.38) * mm});
            skLineSegment(sketch, "E255.30", {"start": v(-106.07, -4.27) * mm, "end": v(-94.35, -4.08) * mm});
            skLineSegment(sketch, "E255.31", {"start": v(-117.8, -4.67) * mm, "end": v(-106.07, -4.27) * mm});
            skLineSegment(sketch, "E255.32", {"start": v(-116.77, 0) * mm, "end": v(-109.84, 0.1) * mm});
            skLineSegment(sketch, "E255.33", {"start": v(-123.7, -0.22) * mm, "end": v(-116.77, 0) * mm});
            skLineSegment(sketch, "E255.34", {"start": v(-129.5, -5.27) * mm, "end": v(-117.8, -4.67) * mm});
            skLineSegment(sketch, "E255.35", {"start": v(-128.92, -0.56) * mm, "end": v(-123.7, -0.22) * mm});
            skLineSegment(sketch, "E255.36", {"start": v(-134.12, -1.03) * mm, "end": v(-128.92, -0.56) * mm});
            skLineSegment(sketch, "E255.37", {"start": v(-137, -5.84) * mm, "end": v(-129.5, -5.27) * mm});
            skLineSegment(sketch, "E255.38", {"start": v(-139.31, -1.64) * mm, "end": v(-134.12, -1.03) * mm});
            skLineSegment(sketch, "E255.39", {"start": v(-155.05, -4.1) * mm, "end": v(-144.49, -2.37) * mm});
            skLineSegment(sketch, "E255.40", {"start": v(-149.84, -7.42) * mm, "end": v(-144.49, -6.65) * mm});
            skLineSegment(sketch, "E255.41", {"start": v(-155.18, -8.27) * mm, "end": v(-149.84, -7.42) * mm});
            skLineSegment(sketch, "E255.42", {"start": v(-161.54, -4.97) * mm, "end": v(-155.05, -4.1) * mm});
            skLineSegment(sketch, "E255.43", {"start": v(-160.52, -9.11) * mm, "end": v(-155.18, -8.27) * mm});
            skLineSegment(sketch, "E255.44", {"start": v(-168.05, -5.64) * mm, "end": v(-161.54, -4.97) * mm});
            skLineSegment(sketch, "E255.45", {"start": v(-165.88, -9.82) * mm, "end": v(-160.52, -9.11) * mm});
            skLineSegment(sketch, "E255.46", {"start": v(-174.58, -6.12) * mm, "end": v(-168.05, -5.64) * mm});
            skLineSegment(sketch, "E255.47", {"start": v(-173.14, -10.5) * mm, "end": v(-165.88, -9.82) * mm});
            skLineSegment(sketch, "E255.48", {"start": v(-181.12, -6.41) * mm, "end": v(-174.58, -6.12) * mm});
            skLineSegment(sketch, "E255.49", {"start": v(-180.42, -10.9) * mm, "end": v(-173.14, -10.5) * mm});
            skLineSegment(sketch, "E255.50", {"start": v(-188.2, -6.52) * mm, "end": v(-181.12, -6.41) * mm});
            skLineSegment(sketch, "E255.51", {"start": v(-187.7, -11.06) * mm, "end": v(-180.42, -10.9) * mm});
            skLineSegment(sketch, "E255.52", {"start": v(-195.27, -6.46) * mm, "end": v(-188.2, -6.52) * mm});
            skLineSegment(sketch, "E255.53", {"start": v(-195, -11.03) * mm, "end": v(-187.7, -11.06) * mm});
            skLineSegment(sketch, "E255.54", {"start": v(-202.34, -6.28) * mm, "end": v(-195.27, -6.46) * mm});
            skLineSegment(sketch, "E255.55", {"start": v(-204.95, -10.76) * mm, "end": v(-195, -11.03) * mm});
            skLineSegment(sketch, "E255.56", {"start": v(-209.42, -6) * mm, "end": v(-202.34, -6.28) * mm});
            skLineSegment(sketch, "E255.57", {"start": v(-214.9, -10.25) * mm, "end": v(-204.95, -10.76) * mm});
            skLineSegment(sketch, "E255.58", {"start": v(-217.79, -5.58) * mm, "end": v(-209.42, -6) * mm});
            skLineSegment(sketch, "E255.59", {"start": v(-224.82, -9.52) * mm, "end": v(-214.9, -10.25) * mm});
            skLineSegment(sketch, "E255.60", {"start": v(-226.15, -5.04) * mm, "end": v(-217.79, -5.58) * mm});
            skLineSegment(sketch, "E255.61", {"start": v(-234.74, -8.57) * mm, "end": v(-224.82, -9.52) * mm});
            skLineSegment(sketch, "E255.62", {"start": v(-234.5, -4.35) * mm, "end": v(-226.15, -5.04) * mm});
            skLineSegment(sketch, "E255.63", {"start": v(-242.83, -3.44) * mm, "end": v(-234.5, -4.35) * mm});
            skLineSegment(sketch, "E255.64", {"start": v(-242.95, -7.65) * mm, "end": v(-234.74, -8.57) * mm});
            skLineSegment(sketch, "E255.65", {"start": v(-252.56, -2.1) * mm, "end": v(-242.83, -3.44) * mm});
            skLineSegment(sketch, "E255.66", {"start": v(-251.15, -6.64) * mm, "end": v(-242.95, -7.65) * mm});
            skLineSegment(sketch, "E255.67", {"start": v(-257.42, -1.44) * mm, "end": v(-252.56, -2.1) * mm});
            skLineSegment(sketch, "E255.68", {"start": v(-259.34, -5.54) * mm, "end": v(-251.15, -6.64) * mm});
            skLineSegment(sketch, "E255.69", {"start": v(-262.3, -0.88) * mm, "end": v(-257.42, -1.44) * mm});
            skLineSegment(sketch, "E255.70", {"start": v(-267.51, -4.31) * mm, "end": v(-259.34, -5.54) * mm});
            skLineSegment(sketch, "E255.71", {"start": v(-269.31, -0.31) * mm, "end": v(-262.3, -0.88) * mm});
            skLineSegment(sketch, "E255.72", {"start": v(-272.2, -3.58) * mm, "end": v(-267.51, -4.31) * mm});
            skLineSegment(sketch, "E255.73", {"start": v(-276.35, 0.03) * mm, "end": v(-269.31, -0.31) * mm});
            skLineSegment(sketch, "E255.74", {"start": v(-276.9, -2.93) * mm, "end": v(-272.2, -3.58) * mm});
            skLineSegment(sketch, "E255.75", {"start": v(-281.6, -2.5) * mm, "end": v(-276.9, -2.93) * mm});
            skLineSegment(sketch, "E255.76", {"start": v(-283.39, 0.18) * mm, "end": v(-276.35, 0.03) * mm});
            skLineSegment(sketch, "E255.77", {"start": v(-283.96, -2.38) * mm, "end": v(-281.6, -2.5) * mm});
            skLineSegment(sketch, "E255.78", {"start": v(-290.43, 0.2) * mm, "end": v(-283.39, 0.18) * mm});
            skLineSegment(sketch, "E255.79", {"start": v(-286.33, -2.38) * mm, "end": v(-283.96, -2.38) * mm});
            skLineSegment(sketch, "E255.80", {"start": v(-288.95, -2.5) * mm, "end": v(-286.33, -2.38) * mm});
            skLineSegment(sketch, "E255.81", {"start": v(-306.85, -0.06) * mm, "end": v(-290.43, 0.2) * mm});
            skLineSegment(sketch, "E255.82", {"start": v(-291.56, -2.75) * mm, "end": v(-288.95, -2.5) * mm});
            skLineSegment(sketch, "E255.83", {"start": v(-296.76, -3.47) * mm, "end": v(-291.56, -2.75) * mm});
            skLineSegment(sketch, "E255.84", {"start": v(-306.85, -5.11) * mm, "end": v(-296.76, -3.47) * mm});
            skLineSegment(sketch, "E255.85", {"start": v(-306.85, -0.06) * mm, "end": v(-306.85, -5.11) * mm});
            skFitSpline(sketch, "E256", {"points": [v(17.05, 0.27) * mm, v(9.79, 0.27) * mm, v(0.55, 0.33) * mm, v(-8.7, 0.27) * mm, v(-17.94, -0.02) * mm, v(-27.17, -0.39) * mm, v(-33.28, -0.58) * mm, v(-39.38, -0.68) * mm, v(-45.49, -0.68) * mm, v(-51.6, -0.55) * mm, v(-65.7, 0.1) * mm, v(-76.73, 0.37) * mm, v(-87.76, 0.38) * mm, v(-109.84, 0.1) * mm, v(-116.77, 0) * mm, v(-123.7, -0.22) * mm, v(-128.92, -0.56) * mm, v(-134.12, -1.03) * mm, v(-139.31, -1.64) * mm, v(-144.49, -2.37) * mm, v(-155.05, -4.1) * mm, v(-161.54, -4.97) * mm, v(-168.05, -5.64) * mm, v(-174.58, -6.12) * mm, v(-181.12, -6.41) * mm, v(-188.2, -6.52) * mm, v(-195.27, -6.46) * mm, v(-202.34, -6.28) * mm, v(-209.42, -6) * mm, v(-217.79, -5.58) * mm, v(-226.15, -5.04) * mm, v(-234.5, -4.35) * mm, v(-242.83, -3.44) * mm, v(-252.56, -2.1) * mm, v(-257.42, -1.44) * mm, v(-262.3, -0.88) * mm, v(-269.31, -0.31) * mm, v(-276.35, 0.03) * mm, v(-283.39, 0.18) * mm, v(-290.43, 0.2) * mm, v(-306.85, -0.06) * mm], "startDerivative": vector(-292.7, -0.66) * mm, "endDerivative": vector(-504.75, -8.84) * mm});
            skFitSpline(sketch, "E257", {"points": [v(-306.85, -5.11) * mm, v(-296.76, -3.47) * mm, v(-291.56, -2.75) * mm, v(-288.95, -2.5) * mm, v(-286.33, -2.38) * mm, v(-283.96, -2.38) * mm, v(-281.6, -2.5) * mm, v(-276.9, -2.93) * mm, v(-272.2, -3.58) * mm, v(-267.51, -4.31) * mm, v(-259.34, -5.54) * mm, v(-251.15, -6.64) * mm, v(-242.95, -7.65) * mm, v(-234.74, -8.57) * mm, v(-224.82, -9.52) * mm, v(-214.9, -10.25) * mm, v(-204.95, -10.76) * mm, v(-195, -11.03) * mm, v(-187.7, -11.06) * mm, v(-180.42, -10.9) * mm, v(-173.14, -10.5) * mm, v(-165.88, -9.82) * mm, v(-160.52, -9.11) * mm, v(-155.18, -8.27) * mm, v(-149.84, -7.42) * mm, v(-144.49, -6.65) * mm, v(-137, -5.84) * mm, v(-129.5, -5.27) * mm, v(-117.8, -4.67) * mm, v(-106.07, -4.27) * mm, v(-94.35, -4.08) * mm, v(-82.62, -4.08) * mm, v(-70.55, -4.28) * mm, v(-58.49, -4.6) * mm, v(-48.3, -4.87) * mm, v(-43.2, -4.93) * mm, v(-38.1, -4.91) * mm, v(-28.72, -4.63) * mm, v(-19.35, -4.19) * mm, v(-8.06, -3.68) * mm, v(-2.42, -3.58) * mm, v(3.22, -3.67) * mm, v(8.34, -3.95) * mm, v(12.79, -4.33) * mm, v(17.13, -4.8) * mm], "startDerivative": vector(394.4, 65.55) * mm, "endDerivative": vector(243.26, -27.2) * mm});
            skSolve(sketch);
        }
        {
            var Q0;
            Q0=sQuery(id+"F1.wireOp",EDGE,"E247");
            cPoint(context, id + "F8", {"entities" : qUnion([Q0]), "parameter" : 0.5});
        }
        {
            var Q0;
            Q0=sQuery(id+"F1.wireOp",EDGE,"E244");
            var Q1;
            Q1 = qCreatedBy(id + "F8" ,VERTEX);
            cPlane(context, id + "F9", {"entities" : qUnion([Q0, Q1]), "cplaneType" : CPlaneType.LINE_POINT, "offset" : 25.4 * mm, "width" : 152.4 * mm, "height" : 152.4 * mm});
        }
        {
            var Q0;
            Q0=qCreatedBy(id+"F9.planeOp",FACE);
            var sketch = newSketch(context, id + "F10", { "sketchPlane" : qUnion([Q0])});
            skLineSegment(sketch, "E258.0", {"start": v(-337.63, -0.09) * mm, "end": v(-327.4, -0.09) * mm});
            skLineSegment(sketch, "E258.1", {"start": v(-337.63, -0.09) * mm, "end": v(-337.63, -5.22) * mm});
            skLineSegment(sketch, "E258.2", {"start": v(-335.7, -4.54) * mm, "end": v(-337.63, -5.22) * mm});
            skLineSegment(sketch, "E258.3", {"start": v(-333.7, -3.95) * mm, "end": v(-335.7, -4.54) * mm});
            skLineSegment(sketch, "E258.4", {"start": v(-331.36, -3.4) * mm, "end": v(-333.7, -3.95) * mm});
            skLineSegment(sketch, "E258.5", {"start": v(-328.88, -3) * mm, "end": v(-331.36, -3.4) * mm});
            skLineSegment(sketch, "E258.6", {"start": v(-326.38, -2.78) * mm, "end": v(-328.88, -3) * mm});
            skLineSegment(sketch, "E258.7", {"start": v(-327.4, -0.09) * mm, "end": v(-321.58, -0.02) * mm});
            skLineSegment(sketch, "E258.8", {"start": v(-323.87, -2.68) * mm, "end": v(-326.38, -2.78) * mm});
            skLineSegment(sketch, "E258.9", {"start": v(-321.35, -2.68) * mm, "end": v(-323.87, -2.68) * mm});
            skLineSegment(sketch, "E258.10", {"start": v(-317.16, -2.8) * mm, "end": v(-321.35, -2.68) * mm});
            skLineSegment(sketch, "E258.11", {"start": v(-321.58, -0.02) * mm, "end": v(-315.77, -0.09) * mm});
            skLineSegment(sketch, "E258.12", {"start": v(-315.77, -0.09) * mm, "end": v(-310.51, -0.35) * mm});
            skLineSegment(sketch, "E258.13", {"start": v(-312.97, -3.06) * mm, "end": v(-317.16, -2.8) * mm});
            skLineSegment(sketch, "E258.14", {"start": v(-308.8, -3.44) * mm, "end": v(-312.97, -3.06) * mm});
            skLineSegment(sketch, "E258.15", {"start": v(-310.51, -0.35) * mm, "end": v(-305.27, -0.8) * mm});
            skLineSegment(sketch, "E258.16", {"start": v(-304.63, -3.94) * mm, "end": v(-308.8, -3.44) * mm});
            skLineSegment(sketch, "E258.17", {"start": v(-296.4, -5.18) * mm, "end": v(-304.63, -3.94) * mm});
            skLineSegment(sketch, "E258.18", {"start": v(-305.27, -0.8) * mm, "end": v(-294.81, -2.07) * mm});
            skLineSegment(sketch, "E258.19", {"start": v(-288.2, -6.64) * mm, "end": v(-296.4, -5.18) * mm});
            skLineSegment(sketch, "E258.20", {"start": v(-294.81, -2.07) * mm, "end": v(-287.26, -3.13) * mm});
            skLineSegment(sketch, "E258.21", {"start": v(-271.85, -9.93) * mm, "end": v(-288.2, -6.64) * mm});
            skLineSegment(sketch, "E258.22", {"start": v(-287.26, -3.13) * mm, "end": v(-279.72, -4.33) * mm});
            skLineSegment(sketch, "E258.23", {"start": v(-279.72, -4.33) * mm, "end": v(-264.7, -7.02) * mm});
            skLineSegment(sketch, "E258.24", {"start": v(-253.17, -13.72) * mm, "end": v(-271.85, -9.93) * mm});
            skLineSegment(sketch, "E258.25", {"start": v(-264.7, -7.02) * mm, "end": v(-236.57, -12.3) * mm});
            skLineSegment(sketch, "E258.26", {"start": v(-243.8, -15.48) * mm, "end": v(-253.17, -13.72) * mm});
            skLineSegment(sketch, "E258.27", {"start": v(-234.4, -17.06) * mm, "end": v(-243.8, -15.48) * mm});
            skLineSegment(sketch, "E258.28", {"start": v(-236.57, -12.3) * mm, "end": v(-229.95, -13.42) * mm});
            skLineSegment(sketch, "E258.29", {"start": v(-223.1, -18.68) * mm, "end": v(-234.4, -17.06) * mm});
            skLineSegment(sketch, "E258.30", {"start": v(-229.95, -13.42) * mm, "end": v(-223.32, -14.43) * mm});
            skLineSegment(sketch, "E258.31", {"start": v(-211.78, -20.01) * mm, "end": v(-223.1, -18.68) * mm});
            skLineSegment(sketch, "E258.32", {"start": v(-223.32, -14.43) * mm, "end": v(-216.67, -15.31) * mm});
            skLineSegment(sketch, "E258.33", {"start": v(-216.67, -15.31) * mm, "end": v(-210, -16.1) * mm});
            skLineSegment(sketch, "E258.34", {"start": v(-200.41, -21.08) * mm, "end": v(-211.78, -20.01) * mm});
            skLineSegment(sketch, "E258.35", {"start": v(-210, -16.1) * mm, "end": v(-198.93, -17.15) * mm});
            skLineSegment(sketch, "E258.36", {"start": v(-189.04, -21.91) * mm, "end": v(-200.41, -21.08) * mm});
            skLineSegment(sketch, "E258.37", {"start": v(-198.93, -17.15) * mm, "end": v(-187.84, -17.94) * mm});
            skLineSegment(sketch, "E258.38", {"start": v(-178.08, -22.53) * mm, "end": v(-189.04, -21.91) * mm});
            skLineSegment(sketch, "E258.39", {"start": v(-187.84, -17.94) * mm, "end": v(-176.73, -18.51) * mm});
            skLineSegment(sketch, "E258.40", {"start": v(-167.11, -22.96) * mm, "end": v(-178.08, -22.53) * mm});
            skLineSegment(sketch, "E258.41", {"start": v(-176.73, -18.51) * mm, "end": v(-165.62, -18.9) * mm});
            skLineSegment(sketch, "E258.42", {"start": v(-156.15, -23.24) * mm, "end": v(-167.11, -22.96) * mm});
            skLineSegment(sketch, "E258.43", {"start": v(-165.62, -18.9) * mm, "end": v(-155.4, -19.08) * mm});
            skLineSegment(sketch, "E258.44", {"start": v(-145.17, -23.35) * mm, "end": v(-156.15, -23.24) * mm});
            skLineSegment(sketch, "E258.45", {"start": v(-155.4, -19.08) * mm, "end": v(-145.16, -19.06) * mm});
            skLineSegment(sketch, "E258.46", {"start": v(-135.55, -23.33) * mm, "end": v(-145.17, -23.35) * mm});
            skLineSegment(sketch, "E258.47", {"start": v(-145.16, -19.06) * mm, "end": v(-127.3, -18.78) * mm});
            skLineSegment(sketch, "E258.48", {"start": v(-125.93, -23.18) * mm, "end": v(-135.55, -23.33) * mm});
            skLineSegment(sketch, "E258.49", {"start": v(-127.3, -18.78) * mm, "end": v(-109.43, -18.24) * mm});
            skLineSegment(sketch, "E258.50", {"start": v(-116.31, -22.91) * mm, "end": v(-125.93, -23.18) * mm});
            skLineSegment(sketch, "E258.51", {"start": v(-106.7, -22.51) * mm, "end": v(-116.31, -22.91) * mm});
            skLineSegment(sketch, "E258.52", {"start": v(-109.43, -18.24) * mm, "end": v(-101.7, -17.89) * mm});
            skLineSegment(sketch, "E258.53", {"start": v(-99.03, -22.1) * mm, "end": v(-106.7, -22.51) * mm});
            skLineSegment(sketch, "E258.54", {"start": v(-101.7, -17.89) * mm, "end": v(-93.98, -17.43) * mm});
            skLineSegment(sketch, "E258.55", {"start": v(-91.37, -21.55) * mm, "end": v(-99.03, -22.1) * mm});
            skLineSegment(sketch, "E258.56", {"start": v(-93.98, -17.43) * mm, "end": v(-86.27, -16.81) * mm});
            skLineSegment(sketch, "E258.57", {"start": v(-83.71, -20.88) * mm, "end": v(-91.37, -21.55) * mm});
            skLineSegment(sketch, "E258.58", {"start": v(-86.27, -16.81) * mm, "end": v(-78.58, -16) * mm});
            skLineSegment(sketch, "E258.59", {"start": v(-76.08, -20.06) * mm, "end": v(-83.71, -20.88) * mm});
            skLineSegment(sketch, "E258.60", {"start": v(-78.58, -16) * mm, "end": v(-70.11, -14.89) * mm});
            skLineSegment(sketch, "E258.61", {"start": v(-69.57, -19.21) * mm, "end": v(-76.08, -20.06) * mm});
            skLineSegment(sketch, "E258.62", {"start": v(-70.11, -14.89) * mm, "end": v(-61.66, -13.57) * mm});
            skLineSegment(sketch, "E258.63", {"start": v(-63.07, -18.25) * mm, "end": v(-69.57, -19.21) * mm});
            skLineSegment(sketch, "E258.64", {"start": v(-61.66, -13.57) * mm, "end": v(-53.24, -12.11) * mm});
            skLineSegment(sketch, "E258.65", {"start": v(-50.13, -16.04) * mm, "end": v(-63.07, -18.25) * mm});
            skLineSegment(sketch, "E258.66", {"start": v(-53.24, -12.11) * mm, "end": v(-44.84, -10.56) * mm});
            skLineSegment(sketch, "E258.67", {"start": v(-34.76, -13.11) * mm, "end": v(-50.13, -16.04) * mm});
            skLineSegment(sketch, "E258.68", {"start": v(-44.84, -10.56) * mm, "end": v(-18.93, -5.78) * mm});
            skLineSegment(sketch, "E258.69", {"start": v(-19.45, -9.93) * mm, "end": v(-34.76, -13.11) * mm});
            skLineSegment(sketch, "E258.70", {"start": v(-18.93, -5.78) * mm, "end": v(-3.6, -3) * mm});
            skLineSegment(sketch, "E258.71", {"start": v(-4.73, -6.75) * mm, "end": v(-19.45, -9.93) * mm});
            skLineSegment(sketch, "E258.72", {"start": v(-3.6, -3) * mm, "end": v(4.1, -1.81) * mm});
            skLineSegment(sketch, "E258.73", {"start": v(2.66, -5.3) * mm, "end": v(-4.73, -6.75) * mm});
            skLineSegment(sketch, "E258.74", {"start": v(4.1, -1.81) * mm, "end": v(7.97, -1.32) * mm});
            skLineSegment(sketch, "E258.75", {"start": v(10.1, -4.12) * mm, "end": v(2.66, -5.3) * mm});
            skLineSegment(sketch, "E258.76", {"start": v(7.97, -1.32) * mm, "end": v(11.84, -0.91) * mm});
            skLineSegment(sketch, "E258.77", {"start": v(13.66, -3.68) * mm, "end": v(10.1, -4.12) * mm});
            skLineSegment(sketch, "E258.78", {"start": v(11.84, -0.91) * mm, "end": v(19.34, -0.36) * mm});
            skLineSegment(sketch, "E258.79", {"start": v(17.24, -3.33) * mm, "end": v(13.66, -3.68) * mm});
            skLineSegment(sketch, "E258.80", {"start": v(24.41, -2.78) * mm, "end": v(17.24, -3.33) * mm});
            skLineSegment(sketch, "E258.81", {"start": v(19.34, -0.36) * mm, "end": v(26.85, 0) * mm});
            skLineSegment(sketch, "E258.82", {"start": v(27.97, -2.54) * mm, "end": v(24.41, -2.78) * mm});
            skLineSegment(sketch, "E258.83", {"start": v(26.85, 0) * mm, "end": v(36.92, 0.4) * mm});
            skLineSegment(sketch, "E258.84", {"start": v(31.54, -2.4) * mm, "end": v(27.97, -2.54) * mm});
            skLineSegment(sketch, "E258.85", {"start": v(35.1, -2.43) * mm, "end": v(31.54, -2.4) * mm});
            skLineSegment(sketch, "E258.86", {"start": v(36.92, 0.4) * mm, "end": v(43.67, 0.45) * mm});
            skLineSegment(sketch, "E258.87", {"start": v(38.64, -2.75) * mm, "end": v(35.1, -2.43) * mm});
            skLineSegment(sketch, "E258.88", {"start": v(41.65, -3.3) * mm, "end": v(38.64, -2.75) * mm});
            skLineSegment(sketch, "E258.89", {"start": v(44.24, -3.93) * mm, "end": v(41.65, -3.3) * mm});
            skLineSegment(sketch, "E258.90", {"start": v(46.74, -4.7) * mm, "end": v(44.24, -3.93) * mm});
            skLineSegment(sketch, "E258.91", {"start": v(46.74, 0.4) * mm, "end": v(46.74, -4.7) * mm});
            skLineSegment(sketch, "E258.92", {"start": v(43.67, 0.45) * mm, "end": v(46.74, 0.4) * mm});
            skFitSpline(sketch, "E259", {"points": [v(-337.63, -0.09) * mm, v(-327.4, -0.09) * mm, v(-321.58, -0.02) * mm, v(-315.77, -0.09) * mm, v(-310.51, -0.35) * mm, v(-305.27, -0.8) * mm, v(-294.81, -2.07) * mm, v(-287.26, -3.13) * mm, v(-279.72, -4.33) * mm, v(-264.7, -7.02) * mm, v(-236.57, -12.3) * mm, v(-229.95, -13.42) * mm, v(-223.32, -14.43) * mm, v(-216.67, -15.31) * mm, v(-210, -16.1) * mm, v(-198.93, -17.15) * mm, v(-187.84, -17.94) * mm, v(-176.73, -18.51) * mm, v(-165.62, -18.9) * mm, v(-155.4, -19.08) * mm, v(-145.16, -19.06) * mm, v(-127.3, -18.78) * mm, v(-109.43, -18.24) * mm, v(-101.7, -17.89) * mm, v(-93.98, -17.43) * mm, v(-86.27, -16.81) * mm, v(-78.58, -16) * mm, v(-70.11, -14.89) * mm, v(-61.66, -13.57) * mm, v(-53.24, -12.11) * mm, v(-44.84, -10.56) * mm, v(-18.93, -5.78) * mm, v(-3.6, -3) * mm, v(4.1, -1.81) * mm, v(7.97, -1.32) * mm, v(11.84, -0.91) * mm, v(19.34, -0.36) * mm, v(26.85, 0) * mm, v(36.92, 0.4) * mm, v(43.67, 0.45) * mm, v(46.74, 0.4) * mm], "startDerivative": vector(415.36, -1.24) * mm, "endDerivative": vector(194.02, -2.88) * mm});
            skFitSpline(sketch, "E260", {"points": [v(46.74, -4.7) * mm, v(44.24, -3.93) * mm, v(41.65, -3.3) * mm, v(38.64, -2.75) * mm, v(35.1, -2.43) * mm, v(31.54, -2.4) * mm, v(27.97, -2.54) * mm, v(24.41, -2.78) * mm, v(17.24, -3.33) * mm, v(13.66, -3.68) * mm, v(10.1, -4.12) * mm, v(2.66, -5.3) * mm, v(-4.73, -6.75) * mm, v(-19.45, -9.93) * mm, v(-34.76, -13.11) * mm, v(-50.13, -16.04) * mm, v(-63.07, -18.25) * mm, v(-69.57, -19.21) * mm, v(-76.08, -20.06) * mm, v(-83.71, -20.88) * mm, v(-91.37, -21.55) * mm, v(-99.03, -22.1) * mm, v(-106.7, -22.51) * mm, v(-116.31, -22.91) * mm, v(-125.93, -23.18) * mm, v(-135.55, -23.33) * mm, v(-145.17, -23.35) * mm, v(-156.15, -23.24) * mm, v(-167.11, -22.96) * mm, v(-178.08, -22.53) * mm, v(-189.04, -21.91) * mm, v(-200.41, -21.08) * mm, v(-211.78, -20.01) * mm, v(-223.1, -18.68) * mm, v(-234.4, -17.06) * mm, v(-243.8, -15.48) * mm, v(-253.17, -13.72) * mm, v(-271.85, -9.93) * mm, v(-288.2, -6.64) * mm, v(-296.4, -5.18) * mm, v(-304.63, -3.94) * mm, v(-308.8, -3.44) * mm, v(-312.97, -3.06) * mm, v(-317.16, -2.8) * mm, v(-321.35, -2.68) * mm, v(-323.87, -2.68) * mm, v(-326.38, -2.78) * mm, v(-328.88, -3) * mm, v(-331.36, -3.4) * mm, v(-333.7, -3.95) * mm, v(-335.7, -4.54) * mm, v(-337.63, -5.22) * mm], "startDerivative": vector(-207.55, 65.48) * mm, "endDerivative": vector(-181.72, -64.91) * mm});
            skSolve(sketch);
        }
        {
            var Q0;
            Q0=sQuery(id+"F1.wireOp",EDGE,"E248");
            cPoint(context, id + "F11", {"entities" : qUnion([Q0]), "parameter" : 0.5});
        }
        {
            var Q0;
            Q0=sQuery(id+"F1.wireOp",EDGE,"E244");
            var Q1;
            Q1 = qCreatedBy(id + "F11" ,VERTEX);
            cPlane(context, id + "F12", {"entities" : qUnion([Q0, Q1]), "cplaneType" : CPlaneType.LINE_POINT, "offset" : 25.4 * mm, "width" : 152.4 * mm, "height" : 152.4 * mm});
        }
        {
            var Q0;
            Q0=qCreatedBy(id+"F12.planeOp",FACE);
            var sketch = newSketch(context, id + "F13", { "sketchPlane" : qUnion([Q0])});
            skLineSegment(sketch, "E261.0", {"start": v(-361.57, -0.07) * mm, "end": v(-361.28, -5.22) * mm});
            skLineSegment(sketch, "E261.1", {"start": v(-361.28, -5.22) * mm, "end": v(-358.86, -4.53) * mm});
            skLineSegment(sketch, "E261.2", {"start": v(-353.32, -0.07) * mm, "end": v(-361.57, -0.07) * mm});
            skLineSegment(sketch, "E261.3", {"start": v(-358.86, -4.53) * mm, "end": v(-356.36, -3.91) * mm});
            skLineSegment(sketch, "E261.4", {"start": v(-356.36, -3.91) * mm, "end": v(-353.47, -3.35) * mm});
            skLineSegment(sketch, "E261.5", {"start": v(-341.39, -0.07) * mm, "end": v(-353.32, -0.07) * mm});
            skLineSegment(sketch, "E261.6", {"start": v(-353.47, -3.35) * mm, "end": v(-349.95, -2.9) * mm});
            skLineSegment(sketch, "E261.7", {"start": v(-349.95, -2.9) * mm, "end": v(-346.42, -2.7) * mm});
            skLineSegment(sketch, "E261.8", {"start": v(-346.42, -2.7) * mm, "end": v(-342.88, -2.7) * mm});
            skLineSegment(sketch, "E261.9", {"start": v(-342.88, -2.7) * mm, "end": v(-339.33, -2.87) * mm});
            skLineSegment(sketch, "E261.10", {"start": v(-338.13, -0.1) * mm, "end": v(-341.39, -0.07) * mm});
            skLineSegment(sketch, "E261.11", {"start": v(-339.33, -2.87) * mm, "end": v(-335.7, -3.18) * mm});
            skLineSegment(sketch, "E261.12", {"start": v(-334.87, -0.28) * mm, "end": v(-338.13, -0.1) * mm});
            skLineSegment(sketch, "E261.13", {"start": v(-331.15, -0.7) * mm, "end": v(-334.87, -0.28) * mm});
            skLineSegment(sketch, "E261.14", {"start": v(-335.7, -3.18) * mm, "end": v(-332.07, -3.62) * mm});
            skLineSegment(sketch, "E261.15", {"start": v(-327.45, -1.3) * mm, "end": v(-331.15, -0.7) * mm});
            skLineSegment(sketch, "E261.16", {"start": v(-332.07, -3.62) * mm, "end": v(-324.85, -4.75) * mm});
            skLineSegment(sketch, "E261.17", {"start": v(-320.1, -2.74) * mm, "end": v(-327.45, -1.3) * mm});
            skLineSegment(sketch, "E261.18", {"start": v(-324.85, -4.75) * mm, "end": v(-315.77, -6.43) * mm});
            skLineSegment(sketch, "E261.19", {"start": v(-307.18, -5.16) * mm, "end": v(-320.1, -2.74) * mm});
            skLineSegment(sketch, "E261.20", {"start": v(-315.77, -6.43) * mm, "end": v(-306.71, -8.23) * mm});
            skLineSegment(sketch, "E261.21", {"start": v(-294.24, -7.4) * mm, "end": v(-307.18, -5.16) * mm});
            skLineSegment(sketch, "E261.22", {"start": v(-306.71, -8.23) * mm, "end": v(-288.4, -11.93) * mm});
            skLineSegment(sketch, "E261.23", {"start": v(-274.54, -10.62) * mm, "end": v(-294.24, -7.4) * mm});
            skLineSegment(sketch, "E261.24", {"start": v(-288.4, -11.93) * mm, "end": v(-280.02, -13.48) * mm});
            skLineSegment(sketch, "E261.25", {"start": v(-280.02, -13.48) * mm, "end": v(-271.62, -14.88) * mm});
            skLineSegment(sketch, "E261.26", {"start": v(-264.68, -12.08) * mm, "end": v(-274.55, -10.62) * mm});
            skLineSegment(sketch, "E261.27", {"start": v(-271.62, -14.88) * mm, "end": v(-261.95, -16.32) * mm});
            skLineSegment(sketch, "E261.28", {"start": v(-254.79, -13.4) * mm, "end": v(-264.68, -12.08) * mm});
            skLineSegment(sketch, "E261.29", {"start": v(-261.95, -16.32) * mm, "end": v(-252.25, -17.6) * mm});
            skLineSegment(sketch, "E261.30", {"start": v(-243.09, -14.79) * mm, "end": v(-254.79, -13.4) * mm});
            skLineSegment(sketch, "E261.31", {"start": v(-252.25, -17.6) * mm, "end": v(-242.24, -18.83) * mm});
            skLineSegment(sketch, "E261.32", {"start": v(-231.37, -15.99) * mm, "end": v(-243.09, -14.79) * mm});
            skLineSegment(sketch, "E261.33", {"start": v(-242.24, -18.83) * mm, "end": v(-232.22, -19.9) * mm});
            skLineSegment(sketch, "E261.34", {"start": v(-219.63, -16.98) * mm, "end": v(-231.37, -15.99) * mm});
            skLineSegment(sketch, "E261.35", {"start": v(-232.22, -19.9) * mm, "end": v(-222.92, -20.75) * mm});
            skLineSegment(sketch, "E261.36", {"start": v(-207.88, -17.75) * mm, "end": v(-219.63, -16.98) * mm});
            skLineSegment(sketch, "E261.37", {"start": v(-222.92, -20.75) * mm, "end": v(-213.61, -21.48) * mm});
            skLineSegment(sketch, "E261.38", {"start": v(-213.61, -21.48) * mm, "end": v(-204.3, -22.08) * mm});
            skLineSegment(sketch, "E261.39", {"start": v(-192.1, -18.47) * mm, "end": v(-207.88, -17.75) * mm});
            skLineSegment(sketch, "E261.40", {"start": v(-204.3, -22.08) * mm, "end": v(-194.97, -22.54) * mm});
            skLineSegment(sketch, "E261.41", {"start": v(-176.3, -18.9) * mm, "end": v(-192.1, -18.47) * mm});
            skLineSegment(sketch, "E261.42", {"start": v(-194.97, -22.54) * mm, "end": v(-182.4, -22.96) * mm});
            skLineSegment(sketch, "E261.43", {"start": v(-182.4, -22.96) * mm, "end": v(-169.82, -23.2) * mm});
            skLineSegment(sketch, "E261.44", {"start": v(-160.5, -19.08) * mm, "end": v(-176.3, -18.9) * mm});
            skLineSegment(sketch, "E261.45", {"start": v(-169.82, -23.2) * mm, "end": v(-144.65, -23.38) * mm});
            skLineSegment(sketch, "E261.46", {"start": v(-144.7, -19.1) * mm, "end": v(-160.5, -19.08) * mm});
            skLineSegment(sketch, "E261.47", {"start": v(-144.65, -23.38) * mm, "end": v(-125.12, -23.39) * mm});
            skLineSegment(sketch, "E261.48", {"start": v(-128.2, -18.97) * mm, "end": v(-144.7, -19.1) * mm});
            skLineSegment(sketch, "E261.49", {"start": v(-111.72, -18.68) * mm, "end": v(-128.2, -18.97) * mm});
            skLineSegment(sketch, "E261.50", {"start": v(-125.12, -23.39) * mm, "end": v(-115.36, -23.32) * mm});
            skLineSegment(sketch, "E261.51", {"start": v(-115.36, -23.32) * mm, "end": v(-105.6, -23.16) * mm});
            skLineSegment(sketch, "E261.52", {"start": v(-95.23, -18.18) * mm, "end": v(-111.72, -18.68) * mm});
            skLineSegment(sketch, "E261.53", {"start": v(-105.6, -23.16) * mm, "end": v(-94.3, -22.84) * mm});
            skLineSegment(sketch, "E261.54", {"start": v(-78.75, -17.44) * mm, "end": v(-95.23, -18.18) * mm});
            skLineSegment(sketch, "E261.55", {"start": v(-94.3, -22.84) * mm, "end": v(-83.01, -22.37) * mm});
            skLineSegment(sketch, "E261.56", {"start": v(-83.01, -22.37) * mm, "end": v(-71.73, -21.69) * mm});
            skLineSegment(sketch, "E261.57", {"start": v(-66.44, -16.7) * mm, "end": v(-78.75, -17.44) * mm});
            skLineSegment(sketch, "E261.58", {"start": v(-71.73, -21.69) * mm, "end": v(-60.47, -20.78) * mm});
            skLineSegment(sketch, "E261.59", {"start": v(-54.14, -15.72) * mm, "end": v(-66.44, -16.7) * mm});
            skLineSegment(sketch, "E261.60", {"start": v(-60.47, -20.78) * mm, "end": v(-52.96, -20.01) * mm});
            skLineSegment(sketch, "E261.61", {"start": v(-41.86, -14.53) * mm, "end": v(-54.14, -15.72) * mm});
            skLineSegment(sketch, "E261.62", {"start": v(-52.96, -20.01) * mm, "end": v(-45.47, -19.11) * mm});
            skLineSegment(sketch, "E261.63", {"start": v(-45.47, -19.11) * mm, "end": v(-38, -18.1) * mm});
            skLineSegment(sketch, "E261.64", {"start": v(-29.6, -13.1) * mm, "end": v(-41.86, -14.53) * mm});
            skLineSegment(sketch, "E261.65", {"start": v(-38, -18.1) * mm, "end": v(-30.53, -17) * mm});
            skLineSegment(sketch, "E261.66", {"start": v(-20.7, -11.89) * mm, "end": v(-29.6, -13.1) * mm});
            skLineSegment(sketch, "E261.67", {"start": v(-30.53, -17) * mm, "end": v(-19.28, -15.17) * mm});
            skLineSegment(sketch, "E261.68", {"start": v(-11.82, -10.51) * mm, "end": v(-20.7, -11.89) * mm});
            skLineSegment(sketch, "E261.69", {"start": v(-19.28, -15.17) * mm, "end": v(-8.06, -13.2) * mm});
            skLineSegment(sketch, "E261.70", {"start": v(-2.96, -8.99) * mm, "end": v(-11.82, -10.51) * mm});
            skLineSegment(sketch, "E261.71", {"start": v(-8.06, -13.2) * mm, "end": v(3.14, -11.08) * mm});
            skLineSegment(sketch, "E261.72", {"start": v(5.87, -7.32) * mm, "end": v(-2.96, -8.99) * mm});
            skLineSegment(sketch, "E261.73", {"start": v(3.14, -11.08) * mm, "end": v(14.32, -8.85) * mm});
            skLineSegment(sketch, "E261.74", {"start": v(18.43, -4.78) * mm, "end": v(5.87, -7.32) * mm});
            skLineSegment(sketch, "E261.75", {"start": v(14.32, -8.85) * mm, "end": v(25.66, -6.55) * mm});
            skLineSegment(sketch, "E261.76", {"start": v(24.72, -3.55) * mm, "end": v(18.43, -4.78) * mm});
            skLineSegment(sketch, "E261.77", {"start": v(25.66, -6.55) * mm, "end": v(31.34, -5.46) * mm});
            skLineSegment(sketch, "E261.78", {"start": v(31.03, -2.46) * mm, "end": v(24.72, -3.55) * mm});
            skLineSegment(sketch, "E261.79", {"start": v(37, -1.59) * mm, "end": v(31.03, -2.46) * mm});
            skLineSegment(sketch, "E261.80", {"start": v(31.34, -5.46) * mm, "end": v(37.04, -4.47) * mm});
            skLineSegment(sketch, "E261.81", {"start": v(37.04, -4.47) * mm, "end": v(41.22, -3.83) * mm});
            skLineSegment(sketch, "E261.82", {"start": v(43, -0.88) * mm, "end": v(37, -1.59) * mm});
            skLineSegment(sketch, "E261.83", {"start": v(41.22, -3.83) * mm, "end": v(45.4, -3.3) * mm});
            skLineSegment(sketch, "E261.84", {"start": v(49.01, -0.34) * mm, "end": v(43, -0.88) * mm});
            skLineSegment(sketch, "E261.85", {"start": v(45.4, -3.3) * mm, "end": v(49.6, -2.94) * mm});
            skLineSegment(sketch, "E261.86", {"start": v(55.04, 0.02) * mm, "end": v(49.01, -0.34) * mm});
            skLineSegment(sketch, "E261.87", {"start": v(49.6, -2.94) * mm, "end": v(53.83, -2.76) * mm});
            skLineSegment(sketch, "E261.88", {"start": v(60.88, 0.2) * mm, "end": v(55.04, 0.02) * mm});
            skLineSegment(sketch, "E261.89", {"start": v(53.83, -2.76) * mm, "end": v(56.22, -2.77) * mm});
            skLineSegment(sketch, "E261.90", {"start": v(56.22, -2.77) * mm, "end": v(58.6, -2.86) * mm});
            skLineSegment(sketch, "E261.91", {"start": v(58.6, -2.86) * mm, "end": v(60.99, -3.04) * mm});
            skLineSegment(sketch, "E261.92", {"start": v(65.98, 0.28) * mm, "end": v(60.88, 0.2) * mm});
            skLineSegment(sketch, "E261.93", {"start": v(60.99, -3.04) * mm, "end": v(63.36, -3.32) * mm});
            skLineSegment(sketch, "E261.94", {"start": v(70.96, 0.27) * mm, "end": v(65.98, 0.28) * mm});
            skLineSegment(sketch, "E261.95", {"start": v(70.96, 0.27) * mm, "end": v(71.25, -4.8) * mm});
            skLineSegment(sketch, "E261.96", {"start": v(68.8, -4.25) * mm, "end": v(71.25, -4.8) * mm});
            skLineSegment(sketch, "E261.97", {"start": v(66.27, -3.77) * mm, "end": v(68.8, -4.25) * mm});
            skLineSegment(sketch, "E261.98", {"start": v(63.36, -3.32) * mm, "end": v(66.27, -3.77) * mm});
            skFitSpline(sketch, "E262", {"points": [v(71.25, -4.8) * mm, v(68.8, -4.25) * mm, v(66.27, -3.77) * mm, v(63.36, -3.32) * mm, v(60.99, -3.04) * mm, v(58.6, -2.86) * mm, v(56.22, -2.77) * mm, v(53.83, -2.76) * mm, v(49.6, -2.94) * mm, v(45.4, -3.3) * mm, v(41.22, -3.83) * mm, v(37.04, -4.47) * mm, v(31.34, -5.46) * mm, v(25.66, -6.55) * mm, v(14.32, -8.85) * mm, v(3.14, -11.08) * mm, v(-8.06, -13.2) * mm, v(-19.28, -15.17) * mm, v(-30.53, -17) * mm, v(-38, -18.1) * mm, v(-45.47, -19.11) * mm, v(-52.96, -20.01) * mm, v(-60.47, -20.78) * mm, v(-71.73, -21.69) * mm, v(-83.01, -22.37) * mm, v(-94.3, -22.84) * mm, v(-105.6, -23.16) * mm, v(-115.36, -23.32) * mm, v(-125.12, -23.39) * mm, v(-144.65, -23.38) * mm, v(-169.82, -23.2) * mm, v(-182.4, -22.96) * mm, v(-194.97, -22.54) * mm, v(-204.3, -22.08) * mm, v(-213.61, -21.48) * mm, v(-222.92, -20.75) * mm, v(-232.22, -19.9) * mm, v(-242.24, -18.83) * mm, v(-252.25, -17.6) * mm, v(-261.95, -16.32) * mm, v(-271.62, -14.88) * mm, v(-280.02, -13.48) * mm, v(-288.4, -11.93) * mm, v(-306.71, -8.23) * mm, v(-315.77, -6.43) * mm, v(-324.85, -4.75) * mm, v(-332.07, -3.62) * mm, v(-335.7, -3.18) * mm, v(-339.33, -2.87) * mm, v(-342.88, -2.7) * mm, v(-346.42, -2.7) * mm, v(-349.95, -2.9) * mm, v(-353.47, -3.35) * mm, v(-356.36, -3.91) * mm, v(-358.86, -4.53) * mm, v(-361.28, -5.22) * mm], "startDerivative": vector(-230.33, 51.79) * mm, "endDerivative": vector(-225.65, -66.27) * mm});
            skLineSegment(sketch, "E263", {"start": v(-361.28, -5.22) * mm, "end": v(-361.57, -0.07) * mm});
            skFitSpline(sketch, "E264", {"points": [v(-361.57, -0.07) * mm, v(-353.32, -0.07) * mm, v(-341.39, -0.07) * mm, v(-338.13, -0.1) * mm, v(-334.87, -0.28) * mm, v(-331.15, -0.7) * mm, v(-327.45, -1.3) * mm, v(-320.1, -2.74) * mm, v(-307.18, -5.16) * mm, v(-294.24, -7.4) * mm, v(-274.54, -10.62) * mm, v(-264.68, -12.08) * mm, v(-254.79, -13.4) * mm, v(-243.09, -14.79) * mm, v(-231.37, -15.99) * mm, v(-219.63, -16.98) * mm, v(-207.88, -17.75) * mm, v(-192.1, -18.47) * mm, v(-176.3, -18.9) * mm, v(-160.5, -19.08) * mm, v(-144.7, -19.1) * mm, v(-128.2, -18.97) * mm, v(-111.72, -18.68) * mm, v(-95.23, -18.18) * mm, v(-78.75, -17.44) * mm, v(-66.44, -16.7) * mm, v(-54.14, -15.72) * mm, v(-41.86, -14.53) * mm, v(-29.6, -13.1) * mm, v(-20.7, -11.89) * mm, v(-11.82, -10.51) * mm, v(-2.96, -8.99) * mm, v(5.87, -7.32) * mm, v(18.43, -4.78) * mm, v(24.72, -3.55) * mm, v(31.03, -2.46) * mm, v(37, -1.59) * mm, v(43, -0.88) * mm, v(49.01, -0.34) * mm, v(55.04, 0.02) * mm, v(60.88, 0.2) * mm, v(65.98, 0.28) * mm, v(70.96, 0.27) * mm], "startDerivative": vector(341.04, -0.14) * mm, "endDerivative": vector(294.76, -1.58) * mm});
            skSolve(sketch);
        }
        {
            var Q0;
            Q0=sQuery(id+"F1.wireOp",EDGE,"E249");
            cPoint(context, id + "F14", {"entities" : qUnion([Q0]), "parameter" : 0.5});
        }
        {
            var Q0;
            Q0=sQuery(id+"F1.wireOp",EDGE,"E244");
            var Q1;
            Q1 = qCreatedBy(id + "F14" ,VERTEX);
            cPlane(context, id + "F15", {"entities" : qUnion([Q0, Q1]), "cplaneType" : CPlaneType.LINE_POINT, "offset" : 25.4 * mm, "width" : 152.4 * mm, "height" : 152.4 * mm});
        }
        {
            var Q0;
            Q0=qCreatedBy(id+"F15.planeOp",FACE);
            var sketch = newSketch(context, id + "F16", { "sketchPlane" : qUnion([Q0])});
            skLineSegment(sketch, "E265.0", {"start": v(-337.37, -0.15) * mm, "end": v(-337.37, -5.22) * mm});
            skLineSegment(sketch, "E265.1", {"start": v(-337.37, -0.15) * mm, "end": v(-324.54, -0.15) * mm});
            skLineSegment(sketch, "E265.2", {"start": v(-335.02, -4.58) * mm, "end": v(-337.37, -5.22) * mm});
            skLineSegment(sketch, "E265.3", {"start": v(-332.59, -4) * mm, "end": v(-335.02, -4.58) * mm});
            skLineSegment(sketch, "E265.4", {"start": v(-329.78, -3.46) * mm, "end": v(-332.59, -4) * mm});
            skLineSegment(sketch, "E265.5", {"start": v(-327.28, -3.1) * mm, "end": v(-329.78, -3.46) * mm});
            skLineSegment(sketch, "E265.6", {"start": v(-324.77, -2.87) * mm, "end": v(-327.28, -3.1) * mm});
            skLineSegment(sketch, "E265.7", {"start": v(-319.73, -2.67) * mm, "end": v(-324.77, -2.87) * mm});
            skLineSegment(sketch, "E265.8", {"start": v(-324.54, -0.15) * mm, "end": v(-314.3, -0.01) * mm});
            skLineSegment(sketch, "E265.9", {"start": v(-314.67, -2.75) * mm, "end": v(-319.73, -2.67) * mm});
            skLineSegment(sketch, "E265.10", {"start": v(-309.62, -2.97) * mm, "end": v(-314.67, -2.75) * mm});
            skLineSegment(sketch, "E265.11", {"start": v(-314.3, -0.01) * mm, "end": v(-309.17, -0.02) * mm});
            skLineSegment(sketch, "E265.12", {"start": v(-303.49, -3.36) * mm, "end": v(-309.62, -2.97) * mm});
            skLineSegment(sketch, "E265.13", {"start": v(-309.17, -0.02) * mm, "end": v(-304.05, -0.15) * mm});
            skLineSegment(sketch, "E265.14", {"start": v(-297.38, -3.9) * mm, "end": v(-303.49, -3.36) * mm});
            skLineSegment(sketch, "E265.15", {"start": v(-304.05, -0.15) * mm, "end": v(-299.28, -0.44) * mm});
            skLineSegment(sketch, "E265.16", {"start": v(-299.28, -0.44) * mm, "end": v(-294.51, -0.86) * mm});
            skLineSegment(sketch, "E265.17", {"start": v(-291, -4.62) * mm, "end": v(-297.38, -3.9) * mm});
            skLineSegment(sketch, "E265.18", {"start": v(-294.51, -0.86) * mm, "end": v(-285, -1.92) * mm});
            skLineSegment(sketch, "E265.19", {"start": v(-284.62, -5.43) * mm, "end": v(-291, -4.62) * mm});
            skLineSegment(sketch, "E265.20", {"start": v(-271.88, -7.15) * mm, "end": v(-284.62, -5.43) * mm});
            skLineSegment(sketch, "E265.21", {"start": v(-285, -1.92) * mm, "end": v(-255.5, -5.44) * mm});
            skLineSegment(sketch, "E265.22", {"start": v(-253.13, -9.67) * mm, "end": v(-271.88, -7.15) * mm});
            skLineSegment(sketch, "E265.23", {"start": v(-255.5, -5.44) * mm, "end": v(-248.31, -6.2) * mm});
            skLineSegment(sketch, "E265.24", {"start": v(-243.74, -10.83) * mm, "end": v(-253.13, -9.67) * mm});
            skLineSegment(sketch, "E265.25", {"start": v(-248.31, -6.2) * mm, "end": v(-241.12, -6.88) * mm});
            skLineSegment(sketch, "E265.26", {"start": v(-234.33, -11.86) * mm, "end": v(-243.74, -10.83) * mm});
            skLineSegment(sketch, "E265.27", {"start": v(-241.12, -6.88) * mm, "end": v(-226.71, -8.03) * mm});
            skLineSegment(sketch, "E265.28", {"start": v(-224.28, -12.78) * mm, "end": v(-234.33, -11.86) * mm});
            skLineSegment(sketch, "E265.29", {"start": v(-226.71, -8.03) * mm, "end": v(-215.9, -8.75) * mm});
            skLineSegment(sketch, "E265.30", {"start": v(-214.21, -13.53) * mm, "end": v(-224.28, -12.78) * mm});
            skLineSegment(sketch, "E265.31", {"start": v(-215.9, -8.75) * mm, "end": v(-205.08, -9.34) * mm});
            skLineSegment(sketch, "E265.32", {"start": v(-204.13, -14.1) * mm, "end": v(-214.21, -13.53) * mm});
            skLineSegment(sketch, "E265.33", {"start": v(-205.08, -9.34) * mm, "end": v(-194.26, -9.82) * mm});
            skLineSegment(sketch, "E265.34", {"start": v(-194.05, -14.5) * mm, "end": v(-204.13, -14.1) * mm});
            skLineSegment(sketch, "E265.35", {"start": v(-194.26, -9.82) * mm, "end": v(-183.43, -10.2) * mm});
            skLineSegment(sketch, "E265.36", {"start": v(-182.15, -14.8) * mm, "end": v(-194.05, -14.5) * mm});
            skLineSegment(sketch, "E265.37", {"start": v(-183.43, -10.2) * mm, "end": v(-174.13, -10.45) * mm});
            skLineSegment(sketch, "E265.38", {"start": v(-170.25, -14.94) * mm, "end": v(-182.15, -14.8) * mm});
            skLineSegment(sketch, "E265.39", {"start": v(-174.13, -10.45) * mm, "end": v(-164.84, -10.6) * mm});
            skLineSegment(sketch, "E265.40", {"start": v(-146.45, -15) * mm, "end": v(-170.25, -14.94) * mm});
            skLineSegment(sketch, "E265.41", {"start": v(-164.84, -10.6) * mm, "end": v(-146.25, -10.72) * mm});
            skLineSegment(sketch, "E265.42", {"start": v(-146.25, -10.72) * mm, "end": v(-133.3, -10.7) * mm});
            skLineSegment(sketch, "E265.43", {"start": v(-123.86, -14.97) * mm, "end": v(-146.45, -15) * mm});
            skLineSegment(sketch, "E265.44", {"start": v(-133.3, -10.7) * mm, "end": v(-120.35, -10.6) * mm});
            skLineSegment(sketch, "E265.45", {"start": v(-112.57, -14.84) * mm, "end": v(-123.86, -14.97) * mm});
            skLineSegment(sketch, "E265.46", {"start": v(-120.35, -10.6) * mm, "end": v(-107.41, -10.35) * mm});
            skLineSegment(sketch, "E265.47", {"start": v(-101.28, -14.55) * mm, "end": v(-112.57, -14.84) * mm});
            skLineSegment(sketch, "E265.48", {"start": v(-107.41, -10.35) * mm, "end": v(-94.48, -9.9) * mm});
            skLineSegment(sketch, "E265.49", {"start": v(-93.76, -14.24) * mm, "end": v(-101.28, -14.55) * mm});
            skLineSegment(sketch, "E265.50", {"start": v(-94.48, -9.9) * mm, "end": v(-85.8, -9.46) * mm});
            skLineSegment(sketch, "E265.51", {"start": v(-86.24, -13.84) * mm, "end": v(-93.76, -14.24) * mm});
            skLineSegment(sketch, "E265.52", {"start": v(-85.8, -9.46) * mm, "end": v(-77.12, -8.92) * mm});
            skLineSegment(sketch, "E265.53", {"start": v(-71.21, -12.83) * mm, "end": v(-86.24, -13.84) * mm});
            skLineSegment(sketch, "E265.54", {"start": v(-77.12, -8.92) * mm, "end": v(-68.45, -8.27) * mm});
            skLineSegment(sketch, "E265.55", {"start": v(-57.73, -11.72) * mm, "end": v(-71.21, -12.83) * mm});
            skLineSegment(sketch, "E265.56", {"start": v(-68.45, -8.27) * mm, "end": v(-59.79, -7.51) * mm});
            skLineSegment(sketch, "E265.57", {"start": v(-59.79, -7.51) * mm, "end": v(-44.4, -5.96) * mm});
            skLineSegment(sketch, "E265.58", {"start": v(-51, -11.07) * mm, "end": v(-57.73, -11.72) * mm});
            skLineSegment(sketch, "E265.59", {"start": v(-44.27, -10.32) * mm, "end": v(-51, -11.07) * mm});
            skLineSegment(sketch, "E265.60", {"start": v(-44.4, -5.96) * mm, "end": v(-29.03, -4.2) * mm});
            skLineSegment(sketch, "E265.61", {"start": v(-37.28, -9.44) * mm, "end": v(-44.27, -10.32) * mm});
            skLineSegment(sketch, "E265.62", {"start": v(-30.3, -8.48) * mm, "end": v(-37.28, -9.44) * mm});
            skLineSegment(sketch, "E265.63", {"start": v(-29.03, -4.2) * mm, "end": v(-15.2, -2.56) * mm});
            skLineSegment(sketch, "E265.64", {"start": v(-16.35, -6.5) * mm, "end": v(-30.3, -8.48) * mm});
            skLineSegment(sketch, "E265.65", {"start": v(-15.2, -2.56) * mm, "end": v(-1.39, -0.78) * mm});
            skLineSegment(sketch, "E265.66", {"start": v(7.2, -3.54) * mm, "end": v(-16.35, -6.5) * mm});
            skLineSegment(sketch, "E265.67", {"start": v(-1.39, -0.78) * mm, "end": v(4.4, 0) * mm});
            skLineSegment(sketch, "E265.68", {"start": v(4.4, 0) * mm, "end": v(7.3, 0.33) * mm});
            skLineSegment(sketch, "E265.69", {"start": v(7.3, 0.33) * mm, "end": v(10.21, 0.56) * mm});
            skLineSegment(sketch, "E265.70", {"start": v(12.17, -2.92) * mm, "end": v(7.2, -3.54) * mm});
            skLineSegment(sketch, "E265.71", {"start": v(10.21, 0.56) * mm, "end": v(13.47, 0.69) * mm});
            skLineSegment(sketch, "E265.72", {"start": v(17.16, -2.4) * mm, "end": v(12.17, -2.92) * mm});
            skLineSegment(sketch, "E265.73", {"start": v(13.47, 0.69) * mm, "end": v(16.73, 0.7) * mm});
            skLineSegment(sketch, "E265.74", {"start": v(22.14, -2.1) * mm, "end": v(17.16, -2.4) * mm});
            skLineSegment(sketch, "E265.75", {"start": v(16.73, 0.7) * mm, "end": v(23.26, 0.56) * mm});
            skLineSegment(sketch, "E265.76", {"start": v(24.64, -2.05) * mm, "end": v(22.14, -2.1) * mm});
            skLineSegment(sketch, "E265.77", {"start": v(23.26, 0.56) * mm, "end": v(30.79, 0.48) * mm});
            skLineSegment(sketch, "E265.78", {"start": v(27.14, -2.1) * mm, "end": v(24.64, -2.05) * mm});
            skLineSegment(sketch, "E265.79", {"start": v(29.51, -2.27) * mm, "end": v(27.14, -2.1) * mm});
            skLineSegment(sketch, "E265.80", {"start": v(30.79, 0.48) * mm, "end": v(37.36, 0.49) * mm});
            skLineSegment(sketch, "E265.81", {"start": v(31.87, -2.53) * mm, "end": v(29.51, -2.27) * mm});
            skLineSegment(sketch, "E265.82", {"start": v(36.56, -3.24) * mm, "end": v(31.87, -2.53) * mm});
            skLineSegment(sketch, "E265.83", {"start": v(37.36, 0.49) * mm, "end": v(43.77, 0.56) * mm});
            skLineSegment(sketch, "E265.84", {"start": v(43.8, -4.52) * mm, "end": v(36.56, -3.24) * mm});
            skLineSegment(sketch, "E265.85", {"start": v(43.77, 0.56) * mm, "end": v(43.8, -4.52) * mm});
            skFitSpline(sketch, "E266", {"points": [v(-337.37, -0.15) * mm, v(-324.54, -0.15) * mm, v(-314.3, -0.01) * mm, v(-309.17, -0.02) * mm, v(-304.05, -0.15) * mm, v(-299.28, -0.44) * mm, v(-294.51, -0.86) * mm, v(-285, -1.92) * mm, v(-255.5, -5.44) * mm, v(-248.31, -6.2) * mm, v(-241.12, -6.88) * mm, v(-226.71, -8.03) * mm, v(-215.9, -8.75) * mm, v(-205.08, -9.34) * mm, v(-194.26, -9.82) * mm, v(-183.43, -10.2) * mm, v(-174.13, -10.45) * mm, v(-164.84, -10.6) * mm, v(-146.25, -10.72) * mm, v(-133.3, -10.7) * mm, v(-120.35, -10.6) * mm, v(-107.41, -10.35) * mm, v(-94.48, -9.9) * mm, v(-85.8, -9.46) * mm, v(-77.12, -8.92) * mm, v(-68.45, -8.27) * mm, v(-59.79, -7.51) * mm, v(-44.4, -5.96) * mm, v(-29.03, -4.2) * mm, v(-15.2, -2.56) * mm, v(-1.39, -0.78) * mm, v(4.4, 0) * mm, v(7.3, 0.33) * mm, v(10.21, 0.56) * mm, v(13.47, 0.69) * mm, v(16.73, 0.7) * mm, v(23.26, 0.56) * mm, v(30.79, 0.48) * mm, v(37.36, 0.49) * mm, v(43.77, 0.56) * mm], "startDerivative": vector(426.9, -1.75) * mm, "endDerivative": vector(300.02, 4.1) * mm});
            skFitSpline(sketch, "E267", {"points": [v(43.8, -4.52) * mm, v(36.56, -3.24) * mm, v(31.87, -2.53) * mm, v(29.51, -2.27) * mm, v(27.14, -2.1) * mm, v(24.64, -2.05) * mm, v(22.14, -2.1) * mm, v(17.16, -2.4) * mm, v(12.17, -2.92) * mm, v(7.2, -3.54) * mm, v(-16.35, -6.5) * mm, v(-30.3, -8.48) * mm, v(-37.28, -9.44) * mm, v(-44.27, -10.32) * mm, v(-51, -11.07) * mm, v(-57.73, -11.72) * mm, v(-71.21, -12.83) * mm, v(-86.24, -13.84) * mm, v(-93.76, -14.24) * mm, v(-101.28, -14.55) * mm, v(-112.57, -14.84) * mm, v(-123.86, -14.97) * mm, v(-146.45, -15) * mm, v(-170.25, -14.94) * mm, v(-182.15, -14.8) * mm, v(-194.05, -14.5) * mm, v(-204.13, -14.1) * mm, v(-214.21, -13.53) * mm, v(-224.28, -12.78) * mm, v(-234.33, -11.86) * mm, v(-243.74, -10.83) * mm, v(-253.13, -9.67) * mm, v(-271.88, -7.15) * mm, v(-284.62, -5.43) * mm, v(-291, -4.62) * mm, v(-297.38, -3.9) * mm, v(-303.49, -3.36) * mm, v(-309.62, -2.97) * mm, v(-314.67, -2.75) * mm, v(-319.73, -2.67) * mm, v(-324.77, -2.87) * mm, v(-327.28, -3.1) * mm, v(-329.78, -3.46) * mm, v(-332.59, -4) * mm, v(-335.02, -4.58) * mm, v(-337.37, -5.22) * mm], "startDerivative": vector(-345.35, 62.8) * mm, "endDerivative": vector(-188.38, -52.61) * mm});
            skSolve(sketch);
        }
        {
            var Q0;
            Q0=sQuery(id+"F1.wireOp",EDGE,"E247");
            cPoint(context, id + "F17", {"entities" : qUnion([Q0]), "parameter" : 0.5});
        }
        {
            var Q0;
            Q0=sQuery(id+"F1.wireOp",EDGE,"E247");
            var Q1;
            Q1 = qCreatedBy(id + "F17" ,VERTEX);
            cPlane(context, id + "F18", {"entities" : qUnion([Q0, Q1]), "cplaneType" : CPlaneType.LINE_POINT, "offset" : 25.4 * mm, "width" : 152.4 * mm, "height" : 152.4 * mm});
        }
        {
            var Q0;
            Q0=qCreatedBy(id+"F18.planeOp",FACE);
            var sketch = newSketch(context, id + "F19", { "sketchPlane" : qUnion([Q0])});
            skLineSegment(sketch, "E268.0", {"start": v(266.62, 0.1) * mm, "end": v(266.62, -4.95) * mm});
            skLineSegment(sketch, "E268.1", {"start": v(262.71, -4.44) * mm, "end": v(266.62, -4.95) * mm});
            skLineSegment(sketch, "E268.2", {"start": v(266.62, 0.1) * mm, "end": v(258.78, 0) * mm});
            skLineSegment(sketch, "E268.3", {"start": v(258.7, -4) * mm, "end": v(262.71, -4.44) * mm});
            skLineSegment(sketch, "E268.4", {"start": v(254.08, -3.64) * mm, "end": v(258.7, -4) * mm});
            skLineSegment(sketch, "E268.5", {"start": v(249.9, -3.45) * mm, "end": v(254.08, -3.64) * mm});
            skLineSegment(sketch, "E268.6", {"start": v(245.74, -3.38) * mm, "end": v(249.9, -3.45) * mm});
            skLineSegment(sketch, "E268.7", {"start": v(237.39, -3.38) * mm, "end": v(245.74, -3.38) * mm});
            skLineSegment(sketch, "E268.8", {"start": v(228.8, -3.42) * mm, "end": v(237.39, -3.38) * mm});
            skLineSegment(sketch, "E268.9", {"start": v(220.2, -3.62) * mm, "end": v(228.8, -3.42) * mm});
            skLineSegment(sketch, "E268.10", {"start": v(211.28, -4.13) * mm, "end": v(220.2, -3.62) * mm});
            skLineSegment(sketch, "E268.11", {"start": v(202.38, -4.9) * mm, "end": v(211.28, -4.13) * mm});
            skLineSegment(sketch, "E268.12", {"start": v(212.04, -0.08) * mm, "end": v(206.3, -0.5) * mm});
            skLineSegment(sketch, "E268.13", {"start": v(219.4, 0.15) * mm, "end": v(212.04, -0.08) * mm});
            skLineSegment(sketch, "E268.14", {"start": v(226.78, 0.14) * mm, "end": v(219.4, 0.15) * mm});
            skLineSegment(sketch, "E268.15", {"start": v(241.53, -0.07) * mm, "end": v(226.78, 0.14) * mm});
            skLineSegment(sketch, "E268.16", {"start": v(258.78, 0) * mm, "end": v(241.53, -0.07) * mm});
            skLineSegment(sketch, "E268.17", {"start": v(206.3, -0.5) * mm, "end": v(200.59, -1.08) * mm});
            skLineSegment(sketch, "E268.18", {"start": v(200.59, -1.08) * mm, "end": v(188.46, -2.41) * mm});
            skLineSegment(sketch, "E268.19", {"start": v(188.46, -2.41) * mm, "end": v(182.4, -3.12) * mm});
            skLineSegment(sketch, "E268.20", {"start": v(192.72, -6) * mm, "end": v(202.38, -4.9) * mm});
            skLineSegment(sketch, "E268.21", {"start": v(183.08, -7.3) * mm, "end": v(192.72, -6) * mm});
            skLineSegment(sketch, "E268.22", {"start": v(182.4, -3.12) * mm, "end": v(176.36, -3.93) * mm});
            skLineSegment(sketch, "E268.23", {"start": v(166.1, -9.84) * mm, "end": v(183.08, -7.3) * mm});
            skLineSegment(sketch, "E268.24", {"start": v(176.36, -3.93) * mm, "end": v(169.4, -5) * mm});
            skLineSegment(sketch, "E268.25", {"start": v(169.4, -5) * mm, "end": v(162.45, -6.18) * mm});
            skLineSegment(sketch, "E268.26", {"start": v(149.15, -12.51) * mm, "end": v(166.1, -9.84) * mm});
            skLineSegment(sketch, "E268.27", {"start": v(162.45, -6.18) * mm, "end": v(148.55, -8.53) * mm});
            skLineSegment(sketch, "E268.28", {"start": v(148.55, -8.53) * mm, "end": v(137.16, -10.23) * mm});
            skLineSegment(sketch, "E268.29", {"start": v(133.61, -14.9) * mm, "end": v(149.15, -12.51) * mm});
            skLineSegment(sketch, "E268.30", {"start": v(137.16, -10.23) * mm, "end": v(125.75, -11.72) * mm});
            skLineSegment(sketch, "E268.31", {"start": v(125.83, -16) * mm, "end": v(133.61, -14.9) * mm});
            skLineSegment(sketch, "E268.32", {"start": v(125.75, -11.72) * mm, "end": v(110.21, -13.5) * mm});
            skLineSegment(sketch, "E268.33", {"start": v(118.04, -17.02) * mm, "end": v(125.83, -16) * mm});
            skLineSegment(sketch, "E268.34", {"start": v(108.05, -18.13) * mm, "end": v(118.04, -17.02) * mm});
            skLineSegment(sketch, "E268.35", {"start": v(110.21, -13.5) * mm, "end": v(94.64, -15) * mm});
            skLineSegment(sketch, "E268.36", {"start": v(98.05, -19.06) * mm, "end": v(108.05, -18.13) * mm});
            skLineSegment(sketch, "E268.37", {"start": v(78.01, -20.61) * mm, "end": v(98.05, -19.06) * mm});
            skLineSegment(sketch, "E268.38", {"start": v(94.64, -15) * mm, "end": v(84.92, -15.83) * mm});
            skLineSegment(sketch, "E268.39", {"start": v(84.92, -15.83) * mm, "end": v(75.2, -16.58) * mm});
            skLineSegment(sketch, "E268.40", {"start": v(61.29, -21.7) * mm, "end": v(78.01, -20.6) * mm});
            skLineSegment(sketch, "E268.41", {"start": v(75.2, -16.58) * mm, "end": v(65.47, -17.22) * mm});
            skLineSegment(sketch, "E268.42", {"start": v(65.47, -17.22) * mm, "end": v(55.73, -17.75) * mm});
            skLineSegment(sketch, "E268.43", {"start": v(44.55, -22.53) * mm, "end": v(61.29, -21.7) * mm});
            skLineSegment(sketch, "E268.44", {"start": v(55.73, -17.75) * mm, "end": v(46.35, -18.15) * mm});
            skLineSegment(sketch, "E268.45", {"start": v(33.56, -22.9) * mm, "end": v(44.55, -22.53) * mm});
            skLineSegment(sketch, "E268.46", {"start": v(46.35, -18.15) * mm, "end": v(36.97, -18.45) * mm});
            skLineSegment(sketch, "E268.47", {"start": v(36.97, -18.45) * mm, "end": v(18.21, -18.9) * mm});
            skLineSegment(sketch, "E268.48", {"start": v(22.56, -23.16) * mm, "end": v(33.56, -22.9) * mm});
            skLineSegment(sketch, "E268.49", {"start": v(0.55, -23.54) * mm, "end": v(22.56, -23.16) * mm});
            skLineSegment(sketch, "E268.50", {"start": v(18.21, -18.9) * mm, "end": v(-1.9, -19.32) * mm});
            skLineSegment(sketch, "E268.51", {"start": v(-17.13, -23.76) * mm, "end": v(0.55, -23.54) * mm});
            skLineSegment(sketch, "E268.52", {"start": v(-1.9, -19.32) * mm, "end": v(-22.01, -19.54) * mm});
            skLineSegment(sketch, "E268.53", {"start": v(-22.01, -19.54) * mm, "end": v(-32.14, -19.53) * mm});
            skLineSegment(sketch, "E268.54", {"start": v(-34.82, -23.79) * mm, "end": v(-17.13, -23.76) * mm});
            skLineSegment(sketch, "E268.55", {"start": v(-32.14, -19.53) * mm, "end": v(-42.28, -19.43) * mm});
            skLineSegment(sketch, "E268.56", {"start": v(-44.94, -23.68) * mm, "end": v(-34.82, -23.79) * mm});
            skLineSegment(sketch, "E268.57", {"start": v(-42.28, -19.43) * mm, "end": v(-52.42, -19.25) * mm});
            skLineSegment(sketch, "E268.58", {"start": v(-55.06, -23.5) * mm, "end": v(-44.94, -23.68) * mm});
            skLineSegment(sketch, "E268.59", {"start": v(-52.42, -19.25) * mm, "end": v(-62.55, -18.98) * mm});
            skLineSegment(sketch, "E268.60", {"start": v(-65.17, -23.2) * mm, "end": v(-55.06, -23.5) * mm});
            skLineSegment(sketch, "E268.61", {"start": v(-75.28, -22.8) * mm, "end": v(-65.17, -23.2) * mm});
            skLineSegment(sketch, "E268.62", {"start": v(-62.55, -18.98) * mm, "end": v(-77.76, -18.37) * mm});
            skLineSegment(sketch, "E268.63", {"start": v(-92.7, -21.84) * mm, "end": v(-75.28, -22.8) * mm});
            skLineSegment(sketch, "E268.64", {"start": v(-77.76, -18.37) * mm, "end": v(-92.95, -17.52) * mm});
            skLineSegment(sketch, "E268.65", {"start": v(-110.1, -20.62) * mm, "end": v(-92.7, -21.84) * mm});
            skLineSegment(sketch, "E268.66", {"start": v(-92.95, -17.52) * mm, "end": v(-106.77, -16.63) * mm});
            skLineSegment(sketch, "E268.67", {"start": v(-106.77, -16.63) * mm, "end": v(-120.6, -15.64) * mm});
            skLineSegment(sketch, "E268.68", {"start": v(-129.38, -19.17) * mm, "end": v(-110.1, -20.62) * mm});
            skLineSegment(sketch, "E268.69", {"start": v(-120.6, -15.64) * mm, "end": v(-134.39, -14.47) * mm});
            skLineSegment(sketch, "E268.70", {"start": v(-139.02, -18.36) * mm, "end": v(-129.38, -19.17) * mm});
            skLineSegment(sketch, "E268.71", {"start": v(-134.39, -14.47) * mm, "end": v(-148.17, -13.08) * mm});
            skLineSegment(sketch, "E268.72", {"start": v(-148.65, -17.41) * mm, "end": v(-139.02, -18.36) * mm});
            skLineSegment(sketch, "E268.73", {"start": v(-148.17, -13.08) * mm, "end": v(-158.48, -11.85) * mm});
            skLineSegment(sketch, "E268.74", {"start": v(-159.27, -16.18) * mm, "end": v(-148.65, -17.41) * mm});
            skLineSegment(sketch, "E268.75", {"start": v(-158.48, -11.85) * mm, "end": v(-168.77, -10.5) * mm});
            skLineSegment(sketch, "E268.76", {"start": v(-169.87, -14.78) * mm, "end": v(-159.27, -16.18) * mm});
            skLineSegment(sketch, "E268.77", {"start": v(-168.77, -10.5) * mm, "end": v(-189.3, -7.55) * mm});
            skLineSegment(sketch, "E268.78", {"start": v(-183.53, -12.86) * mm, "end": v(-169.87, -14.78) * mm});
            skLineSegment(sketch, "E268.79", {"start": v(-190.35, -11.83) * mm, "end": v(-183.53, -12.86) * mm});
            skLineSegment(sketch, "E268.80", {"start": v(-189.3, -7.55) * mm, "end": v(-205.4, -5.23) * mm});
            skLineSegment(sketch, "E268.81", {"start": v(-197.16, -10.68) * mm, "end": v(-190.35, -11.83) * mm});
            skLineSegment(sketch, "E268.82", {"start": v(-219.59, -6.5) * mm, "end": v(-197.16, -10.68) * mm});
            skLineSegment(sketch, "E268.83", {"start": v(-205.4, -5.23) * mm, "end": v(-213.44, -4.02) * mm});
            skLineSegment(sketch, "E268.84", {"start": v(-213.44, -4.02) * mm, "end": v(-221.46, -2.71) * mm});
            skLineSegment(sketch, "E268.85", {"start": v(-228.12, -5.12) * mm, "end": v(-219.59, -6.5) * mm});
            skLineSegment(sketch, "E268.86", {"start": v(-221.46, -2.71) * mm, "end": v(-233.12, -0.77) * mm});
            skLineSegment(sketch, "E268.87", {"start": v(-232.4, -4.57) * mm, "end": v(-228.12, -5.12) * mm});
            skLineSegment(sketch, "E268.88", {"start": v(-233.12, -0.77) * mm, "end": v(-236.85, -0.28) * mm});
            skLineSegment(sketch, "E268.89", {"start": v(-236.7, -4.1) * mm, "end": v(-232.4, -4.57) * mm});
            skLineSegment(sketch, "E268.90", {"start": v(-236.85, -0.28) * mm, "end": v(-240.6, 0.03) * mm});
            skLineSegment(sketch, "E268.91", {"start": v(-241.19, -3.73) * mm, "end": v(-236.7, -4.1) * mm});
            skLineSegment(sketch, "E268.92", {"start": v(-240.6, 0.03) * mm, "end": v(-243.94, 0.14) * mm});
            skLineSegment(sketch, "E268.93", {"start": v(-245.69, -3.47) * mm, "end": v(-241.19, -3.73) * mm});
            skLineSegment(sketch, "E268.94", {"start": v(-243.94, 0.14) * mm, "end": v(-247.28, 0.14) * mm});
            skLineSegment(sketch, "E268.95", {"start": v(-247.28, 0.14) * mm, "end": v(-253.97, 0.02) * mm});
            skLineSegment(sketch, "E268.96", {"start": v(-250.18, -3.4) * mm, "end": v(-245.69, -3.47) * mm});
            skLineSegment(sketch, "E268.97", {"start": v(-254.68, -3.56) * mm, "end": v(-250.18, -3.4) * mm});
            skLineSegment(sketch, "E268.98", {"start": v(-253.97, 0.02) * mm, "end": v(-266, 0.02) * mm});
            skLineSegment(sketch, "E268.99", {"start": v(-258.85, -3.96) * mm, "end": v(-254.68, -3.56) * mm});
            skLineSegment(sketch, "E268.100", {"start": v(-262.48, -4.46) * mm, "end": v(-258.85, -3.96) * mm});
            skLineSegment(sketch, "E268.101", {"start": v(-266, -5.08) * mm, "end": v(-262.48, -4.46) * mm});
            skLineSegment(sketch, "E268.102", {"start": v(-266, 0.1) * mm, "end": v(-266, -5.08) * mm});
            skFitSpline(sketch, "E269", {"points": [v(266.62, 0.1) * mm, v(258.78, 0) * mm, v(241.53, -0.07) * mm, v(226.78, 0.14) * mm, v(219.4, 0.15) * mm, v(212.04, -0.08) * mm, v(206.3, -0.5) * mm, v(200.59, -1.08) * mm, v(188.46, -2.41) * mm, v(182.4, -3.12) * mm, v(176.36, -3.93) * mm, v(169.4, -5) * mm, v(162.45, -6.18) * mm, v(148.55, -8.53) * mm, v(137.16, -10.23) * mm, v(125.75, -11.72) * mm, v(110.21, -13.5) * mm, v(94.64, -15) * mm, v(84.92, -15.83) * mm, v(75.2, -16.58) * mm, v(65.47, -17.22) * mm, v(55.73, -17.75) * mm, v(46.35, -18.15) * mm, v(36.97, -18.45) * mm, v(18.21, -18.9) * mm, v(-1.9, -19.32) * mm, v(-22.01, -19.54) * mm, v(-32.14, -19.53) * mm, v(-42.28, -19.43) * mm, v(-52.42, -19.25) * mm, v(-62.55, -18.98) * mm, v(-77.76, -18.37) * mm, v(-92.95, -17.52) * mm, v(-106.77, -16.63) * mm, v(-120.6, -15.64) * mm, v(-134.39, -14.47) * mm, v(-148.17, -13.08) * mm, v(-158.48, -11.85) * mm, v(-168.77, -10.5) * mm, v(-189.3, -7.55) * mm, v(-205.4, -5.23) * mm, v(-213.44, -4.02) * mm, v(-221.46, -2.71) * mm, v(-233.12, -0.77) * mm, v(-236.85, -0.28) * mm, v(-240.6, 0.03) * mm, v(-243.94, 0.14) * mm, v(-247.28, 0.14) * mm, v(-253.97, 0.02) * mm, v(-266, 0.1) * mm], "startDerivative": vector(-396.5, -5.91) * mm, "endDerivative": vector(-580.77, 7.57) * mm});
            skFitSpline(sketch, "E270", {"points": [v(-266, -5.08) * mm, v(-262.48, -4.46) * mm, v(-258.85, -3.96) * mm, v(-254.68, -3.56) * mm, v(-250.18, -3.4) * mm, v(-245.69, -3.47) * mm, v(-241.19, -3.73) * mm, v(-236.7, -4.1) * mm, v(-232.4, -4.57) * mm, v(-228.12, -5.12) * mm, v(-219.59, -6.5) * mm, v(-197.16, -10.68) * mm, v(-190.35, -11.83) * mm, v(-183.53, -12.86) * mm, v(-169.87, -14.78) * mm, v(-159.27, -16.18) * mm, v(-148.65, -17.41) * mm, v(-139.02, -18.36) * mm, v(-129.38, -19.17) * mm, v(-110.1, -20.62) * mm, v(-92.7, -21.84) * mm, v(-75.28, -22.8) * mm, v(-65.17, -23.2) * mm, v(-55.06, -23.5) * mm, v(-44.94, -23.68) * mm, v(-34.82, -23.79) * mm, v(-17.13, -23.76) * mm, v(0.55, -23.54) * mm, v(22.56, -23.16) * mm, v(33.56, -22.9) * mm, v(44.55, -22.53) * mm, v(61.29, -21.7) * mm, v(78.01, -20.6) * mm, v(98.05, -19.06) * mm, v(108.05, -18.13) * mm, v(118.04, -17.02) * mm, v(125.83, -16) * mm, v(133.61, -14.9) * mm, v(149.15, -12.51) * mm, v(166.1, -9.84) * mm, v(183.08, -7.3) * mm, v(192.72, -6) * mm, v(202.38, -4.9) * mm, v(211.28, -4.13) * mm, v(220.2, -3.62) * mm, v(228.8, -3.42) * mm, v(237.39, -3.38) * mm, v(245.74, -3.38) * mm, v(249.9, -3.45) * mm, v(254.08, -3.64) * mm, v(258.7, -4) * mm, v(262.71, -4.44) * mm, v(266.62, -4.95) * mm], "startDerivative": vector(300.04, 55.12) * mm, "endDerivative": vector(318.09, -42.94) * mm});
            skSolve(sketch);
        }
        {
            var Q0;
            Q0=makeQuery(id+"F19.imprint","IMPRINT",FACE,{"disambiguationData":[TD([[makeQuery(id+"F19.imprint","IMPRINT",EDGE,{"derivedFrom":sQuery(id+"F19.wireOp",EDGE,"E268.12")}),1.0]])]});
            extrude(context, id + "F20", {"entities" : qUnion([Q0]), "depth" : 431.8 * mm, "offsetDistance" : 25.4 * mm, "symmetric" : true});
        }
        {
            var Q0;
            {var subQ51=sQuery(id+"F16.wireOp",EDGE,"E265.11");Q0=makeQuery(id+"F16.imprint","IMPRINT",FACE,{"disambiguationData":[TD([[makeQuery(id+"F16.imprint","IMPRINT",EDGE,{"derivedFrom":subQ51}),-1.0]])]});}
            extrude(context, id + "F21", {"entities" : qUnion([Q0]), "depth" : 203.2 * mm, "offsetDistance" : 25.4 * mm, "symmetric" : true});
        }
        {
            var Q0;
            Q0 = qSketchRegion(id + "F13", true);
            extrude(context, id + "F22", {"entities" : qUnion([Q0]), "depth" : 101.6 * mm, "offsetDistance" : 25.4 * mm, "symmetric" : true});
        }
        {
            var Q0;
            Q0 = qSketchRegion(id + "F10", true);
            extrude(context, id + "F23", {"entities" : qUnion([Q0]), "depth" : 101.6 * mm, "offsetDistance" : 25.4 * mm, "symmetric" : true});
        }
        {
            var Q0;
            Q0 = qSketchRegion(id + "F6", true);
            extrude(context, id + "F24", {"entities" : qUnion([Q0]), "depth" : 101.6 * mm, "offsetDistance" : 25.4 * mm, "symmetric" : true});
        }
        {
            var Q0;
            Q0 = qSketchRegion(id + "F6", true);
            extrude(context, id + "F25", {"entities" : qUnion([Q0]), "depth" : 101.6 * mm, "offsetDistance" : 25.4 * mm, "symmetric" : true});
        }
        {
            var Q0;
            Q0 = qSketchRegion(id + "F7", true);
            extrude(context, id + "F26", {"entities" : qUnion([Q0]), "depth" : 127 * mm, "offsetDistance" : 25.4 * mm, "symmetric" : true});
        }
    });
